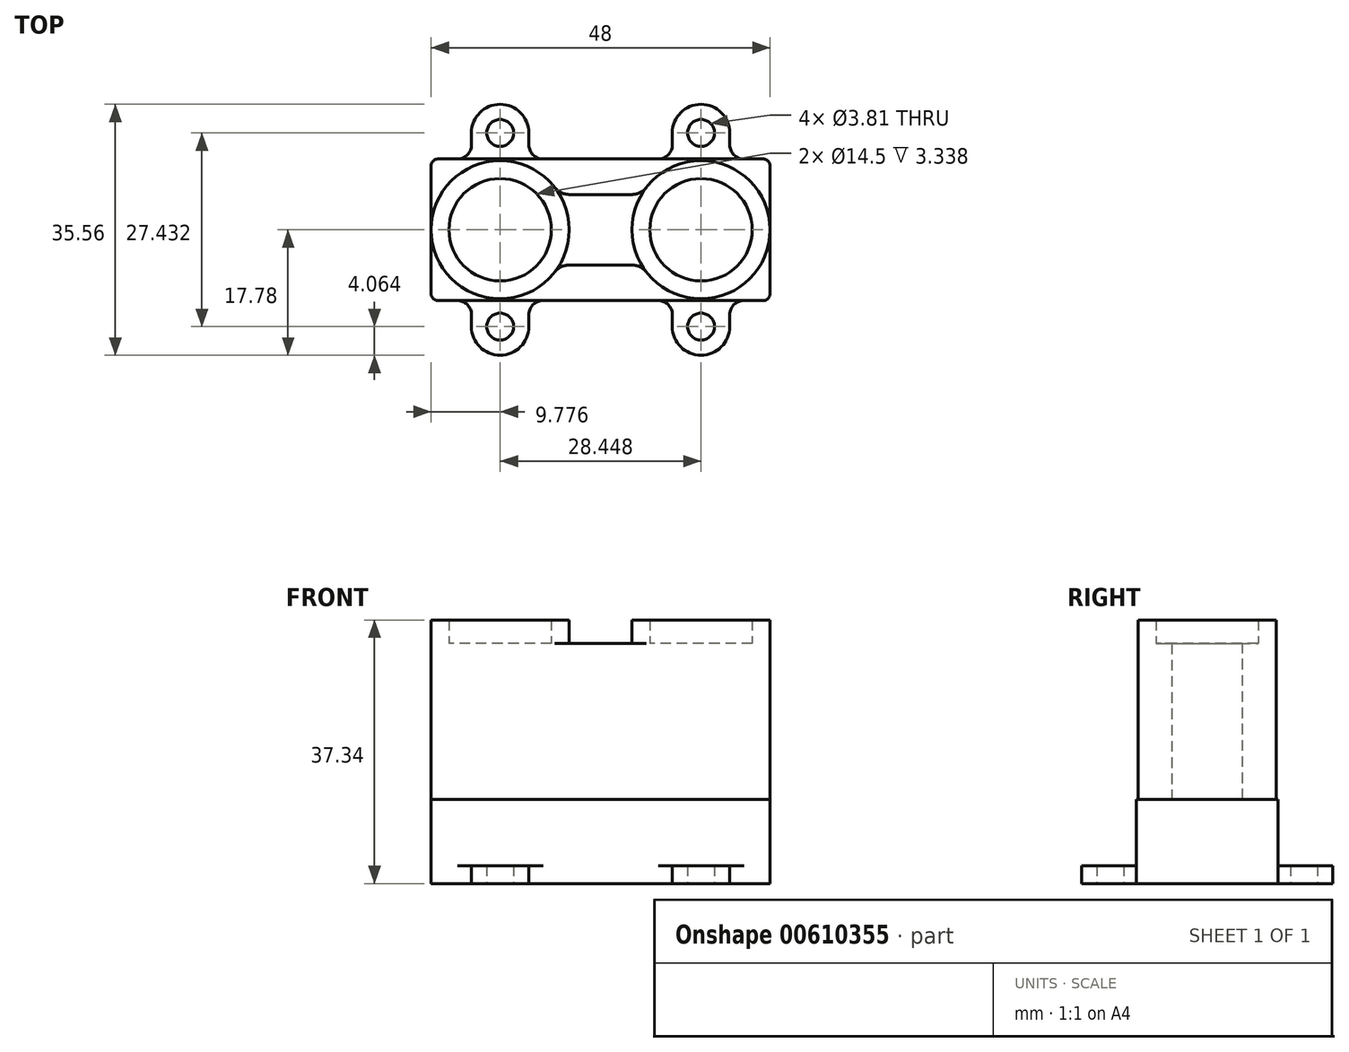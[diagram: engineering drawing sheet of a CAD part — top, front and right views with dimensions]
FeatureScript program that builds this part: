
annotation { "Feature Type Name" : "Feature", "Feature Type Description" : "" }
export const myFeature = defineFeature(function(context is Context, id is Id, definition is map)
    precondition{}
    {
        {
            var Q0;
            Q0=qCreatedBy(makeId("Top.planeOp"),FACE);
            var sketch = newSketch(context, id + "F0", { "sketchPlane" : qUnion([Q0])});
            skLineSegment(sketch, "E0.bottom", {"start": v(24, -10.03) * mm, "end": v(-24, -10.03) * mm});
            skLineSegment(sketch, "E0.top", {"start": v(24, 10.03) * mm, "end": v(-24, 10.03) * mm});
            skLineSegment(sketch, "E0.left", {"start": v(24, -10.03) * mm, "end": v(24, 10.03) * mm});
            skLineSegment(sketch, "E0.right", {"start": v(-24, -10.03) * mm, "end": v(-24, 10.03) * mm});
            skPoint(sketch, "E0.middle", {"position": v(0, 0) * mm});
            skLineSegment(sketch, "E1.bottom", {"start": v(24, -17.78) * mm, "end": v(-24, -17.78) * mm});
            skLineSegment(sketch, "E1.top", {"start": v(24, 17.78) * mm, "end": v(-24, 17.78) * mm});
            skLineSegment(sketch, "E1.left", {"start": v(24, -17.78) * mm, "end": v(24, 17.78) * mm});
            skLineSegment(sketch, "E1.right", {"start": v(-24, -17.78) * mm, "end": v(-24, 17.78) * mm});
            skLineSegment(sketch, "E2.bottom", {"start": v(14.22, -13.72) * mm, "end": v(-14.22, -13.72) * mm, "construction": true});
            skLineSegment(sketch, "E2.top", {"start": v(14.22, 13.72) * mm, "end": v(-14.22, 13.72) * mm, "construction": true});
            skLineSegment(sketch, "E2.left", {"start": v(14.22, -13.72) * mm, "end": v(14.22, 13.72) * mm, "construction": true});
            skLineSegment(sketch, "E2.right", {"start": v(-14.22, -13.72) * mm, "end": v(-14.22, 13.72) * mm, "construction": true});
            skCircle(sketch, "E3", {"center": v(-14.22, 13.72) * mm, "radius": 1.9 * mm});
            skCircle(sketch, "E4", {"center": v(14.22, 13.72) * mm, "radius": 1.9 * mm});
            skCircle(sketch, "E5", {"center": v(14.22, -13.72) * mm, "radius": 1.9 * mm});
            skCircle(sketch, "E6", {"center": v(-14.22, -13.72) * mm, "radius": 1.9 * mm});
            skCircle(sketch, "E7", {"center": v(-14.22, 13.72) * mm, "radius": 4.06 * mm});
            skCircle(sketch, "E8", {"center": v(14.22, 13.72) * mm, "radius": 4.06 * mm});
            skCircle(sketch, "E9", {"center": v(14.22, -13.72) * mm, "radius": 4.06 * mm});
            skCircle(sketch, "E10", {"center": v(-14.22, -13.72) * mm, "radius": 4.06 * mm});
            skLineSegment(sketch, "E11.bottom", {"start": v(-10.16, 13.72) * mm, "end": v(-18.29, 13.72) * mm});
            skLineSegment(sketch, "E11.top", {"start": v(-10.16, 6.35) * mm, "end": v(-18.29, 6.35) * mm});
            skLineSegment(sketch, "E11.left", {"start": v(-10.16, 13.72) * mm, "end": v(-10.16, 6.35) * mm});
            skLineSegment(sketch, "E11.right", {"start": v(-18.29, 13.72) * mm, "end": v(-18.29, 6.35) * mm});
            skPoint(sketch, "E11.middle", {"position": v(-14.22, 10.03) * mm});
            skLineSegment(sketch, "E12.bottom", {"start": v(18.29, 13.72) * mm, "end": v(10.16, 13.72) * mm});
            skLineSegment(sketch, "E12.top", {"start": v(18.29, 6.35) * mm, "end": v(10.16, 6.35) * mm});
            skLineSegment(sketch, "E12.left", {"start": v(18.29, 13.72) * mm, "end": v(18.29, 6.35) * mm});
            skLineSegment(sketch, "E12.right", {"start": v(10.16, 13.72) * mm, "end": v(10.16, 6.35) * mm});
            skPoint(sketch, "E12.middle", {"position": v(14.22, 10.03) * mm});
            skLineSegment(sketch, "E13.bottom", {"start": v(10.16, -13.72) * mm, "end": v(18.29, -13.72) * mm});
            skLineSegment(sketch, "E13.top", {"start": v(10.16, -6.35) * mm, "end": v(18.29, -6.35) * mm});
            skLineSegment(sketch, "E13.left", {"start": v(10.16, -13.72) * mm, "end": v(10.16, -6.35) * mm});
            skLineSegment(sketch, "E13.right", {"start": v(18.29, -13.72) * mm, "end": v(18.29, -6.35) * mm});
            skPoint(sketch, "E13.middle", {"position": v(14.22, -10.03) * mm});
            skLineSegment(sketch, "E14.bottom", {"start": v(-10.16, -13.72) * mm, "end": v(-18.29, -13.72) * mm});
            skLineSegment(sketch, "E14.top", {"start": v(-10.16, -6.35) * mm, "end": v(-18.29, -6.35) * mm});
            skLineSegment(sketch, "E14.left", {"start": v(-10.16, -13.72) * mm, "end": v(-10.16, -6.35) * mm});
            skLineSegment(sketch, "E14.right", {"start": v(-18.29, -13.72) * mm, "end": v(-18.29, -6.35) * mm});
            skPoint(sketch, "E14.middle", {"position": v(-14.22, -10.03) * mm});
            skCircle(sketch, "E15", {"center": v(14.22, 0) * mm, "radius": 9.78 * mm});
            skCircle(sketch, "E16", {"center": v(-14.22, 0) * mm, "radius": 9.78 * mm});
            skLineSegment(sketch, "E17.bottom", {"start": v(9.52, -5) * mm, "end": v(-9.52, -5) * mm});
            skLineSegment(sketch, "E17.top", {"start": v(9.52, 5) * mm, "end": v(-9.52, 5) * mm});
            skLineSegment(sketch, "E17.left", {"start": v(9.52, -5) * mm, "end": v(9.52, 5) * mm});
            skLineSegment(sketch, "E17.right", {"start": v(-9.52, -5) * mm, "end": v(-9.52, 5) * mm});
            skCircle(sketch, "E18", {"center": v(-14.22, 0) * mm, "radius": 7.25 * mm});
            skCircle(sketch, "E19", {"center": v(14.22, 0) * mm, "radius": 7.25 * mm});
            skLineSegment(sketch, "E20", {"start": v(24, -10.03) * mm, "end": v(-3.5, -10.03) * mm, "construction": true});
            skLineSegment(sketch, "E21.bottom", {"start": v(-3.5, -10.03) * mm, "end": v(7.5, -10.03) * mm, "construction": true});
            skLineSegment(sketch, "E21.top", {"start": v(-3.5, -13.03) * mm, "end": v(7.5, -13.03) * mm, "construction": true});
            skLineSegment(sketch, "E21.left", {"start": v(-3.5, -10.03) * mm, "end": v(-3.5, -13.03) * mm, "construction": true});
            skLineSegment(sketch, "E21.right", {"start": v(7.5, -10.03) * mm, "end": v(7.5, -13.03) * mm, "construction": true});
            skSolve(sketch);
        }
        {
            var Q0;
            {var subQ0=sQuery(id+"F0.wireOp",EDGE,"E12.bottom");var subQ3=sQuery(id+"F0.wireOp",EDGE,"E4");var subQ4=makeQuery(id+"F0.imprint","INTERSECT",VERTEX,{"disambiguationData":[OD(0.0)],"derivedFrom":[subQ3,subQ0]});Q0=makeQuery(id+"F0.imprint","IMPRINT",FACE,{"disambiguationData":[TD([[makeQuery(id+"F0.imprint","IMPRINT",EDGE,{"disambiguationData":[TD([[subQ4,-1.0]])],"derivedFrom":subQ3}),-1.0]])]});}
            var Q1;
            {var subQ0=sQuery(id+"F0.wireOp",EDGE,"E11.bottom");var subQ5=sQuery(id+"F0.wireOp",EDGE,"E3");var subQ6=makeQuery(id+"F0.imprint","INTERSECT",VERTEX,{"disambiguationData":[OD(0.0)],"derivedFrom":[subQ5,subQ0]});Q1=makeQuery(id+"F0.imprint","IMPRINT",FACE,{"disambiguationData":[TD([[makeQuery(id+"F0.imprint","IMPRINT",EDGE,{"disambiguationData":[TD([[subQ6,-1.0]])],"derivedFrom":subQ5}),-1.0]])]});}
            var Q2;
            {var subQ0=sQuery(id+"F0.wireOp",EDGE,"E14.bottom");var subQ5=sQuery(id+"F0.wireOp",EDGE,"E6");var subQ6=makeQuery(id+"F0.imprint","INTERSECT",VERTEX,{"disambiguationData":[OD(0.0)],"derivedFrom":[subQ5,subQ0]});Q2=makeQuery(id+"F0.imprint","IMPRINT",FACE,{"disambiguationData":[TD([[makeQuery(id+"F0.imprint","IMPRINT",EDGE,{"disambiguationData":[TD([[subQ6,1.0]])],"derivedFrom":subQ5}),-1.0]])]});}
            var Q3;
            {var subQ0=sQuery(id+"F0.wireOp",EDGE,"E13.bottom");var subQ3=sQuery(id+"F0.wireOp",EDGE,"E5");var subQ4=makeQuery(id+"F0.imprint","INTERSECT",VERTEX,{"disambiguationData":[OD(0.0)],"derivedFrom":[subQ3,subQ0]});Q3=makeQuery(id+"F0.imprint","IMPRINT",FACE,{"disambiguationData":[TD([[makeQuery(id+"F0.imprint","IMPRINT",EDGE,{"disambiguationData":[TD([[subQ4,-1.0]])],"derivedFrom":subQ3}),-1.0]])]});}
            var Q4;
            {var subQ1=sQuery(id+"F0.wireOp",EDGE,"E9");var subQ3=sQuery(id+"F0.wireOp",EDGE,"E0.bottom");var subQ6=makeQuery(id+"F0.imprint","INTERSECT",VERTEX,{"disambiguationData":[OD(0.0)],"derivedFrom":[subQ3,subQ1]});Q4=makeQuery(id+"F0.imprint","IMPRINT",FACE,{"disambiguationData":[TD([[makeQuery(id+"F0.imprint","IMPRINT",EDGE,{"disambiguationData":[TD([[subQ6,-1.0]])],"derivedFrom":subQ3}),1.0]])]});}
            var Q5;
            {var subQ0=sQuery(id+"F0.wireOp",EDGE,"E13.right");var subQ1=sQuery(id+"F0.wireOp",EDGE,"E0.bottom");var subQ2=makeQuery(id+"F0.imprint","INTERSECT",VERTEX,{"derivedFrom":[subQ1,subQ0]});Q5=makeQuery(id+"F0.imprint","IMPRINT",FACE,{"disambiguationData":[TD([[makeQuery(id+"F0.imprint","IMPRINT",EDGE,{"disambiguationData":[TD([[subQ2,-1.0]])],"derivedFrom":subQ1}),1.0]])]});}
            var Q6;
            {var subQ0=sQuery(id+"F0.wireOp",EDGE,"E9");var subQ1=sQuery(id+"F0.wireOp",EDGE,"E0.bottom");var subQ2=makeQuery(id+"F0.imprint","INTERSECT",VERTEX,{"disambiguationData":[OD(1.0)],"derivedFrom":[subQ1,subQ0]});Q6=makeQuery(id+"F0.imprint","IMPRINT",FACE,{"disambiguationData":[TD([[makeQuery(id+"F0.imprint","IMPRINT",EDGE,{"disambiguationData":[TD([[subQ2,-1.0]])],"derivedFrom":subQ1}),1.0]])]});}
            var Q7;
            {var subQ1=sQuery(id+"F0.wireOp",EDGE,"E10");var subQ3=sQuery(id+"F0.wireOp",EDGE,"E0.bottom");var subQ6=makeQuery(id+"F0.imprint","INTERSECT",VERTEX,{"disambiguationData":[OD(0.0)],"derivedFrom":[subQ3,subQ1]});Q7=makeQuery(id+"F0.imprint","IMPRINT",FACE,{"disambiguationData":[TD([[makeQuery(id+"F0.imprint","IMPRINT",EDGE,{"disambiguationData":[TD([[subQ6,-1.0]])],"derivedFrom":subQ3}),1.0]])]});}
            var Q8;
            {var subQ0=sQuery(id+"F0.wireOp",EDGE,"E10");var subQ1=sQuery(id+"F0.wireOp",EDGE,"E0.bottom");var subQ2=makeQuery(id+"F0.imprint","INTERSECT",VERTEX,{"disambiguationData":[OD(1.0)],"derivedFrom":[subQ1,subQ0]});Q8=makeQuery(id+"F0.imprint","IMPRINT",FACE,{"disambiguationData":[TD([[makeQuery(id+"F0.imprint","IMPRINT",EDGE,{"disambiguationData":[TD([[subQ2,-1.0]])],"derivedFrom":subQ1}),1.0]])]});}
            var Q9;
            {var subQ0=sQuery(id+"F0.wireOp",EDGE,"E14.left");var subQ1=sQuery(id+"F0.wireOp",EDGE,"E0.bottom");var subQ2=makeQuery(id+"F0.imprint","INTERSECT",VERTEX,{"derivedFrom":[subQ1,subQ0]});Q9=makeQuery(id+"F0.imprint","IMPRINT",FACE,{"disambiguationData":[TD([[makeQuery(id+"F0.imprint","IMPRINT",EDGE,{"disambiguationData":[TD([[subQ2,-1.0]])],"derivedFrom":subQ1}),1.0]])]});}
            var Q10;
            {var subQ1=sQuery(id+"F0.wireOp",EDGE,"E8");var subQ3=sQuery(id+"F0.wireOp",EDGE,"E0.top");var subQ4=makeQuery(id+"F0.imprint","INTERSECT",VERTEX,{"disambiguationData":[OD(0.0)],"derivedFrom":[subQ3,subQ1]});Q10=makeQuery(id+"F0.imprint","IMPRINT",FACE,{"disambiguationData":[TD([[makeQuery(id+"F0.imprint","IMPRINT",EDGE,{"disambiguationData":[TD([[subQ4,-1.0]])],"derivedFrom":subQ3}),-1.0]])]});}
            var Q11;
            {var subQ1=sQuery(id+"F0.wireOp",EDGE,"E7");var subQ3=sQuery(id+"F0.wireOp",EDGE,"E0.top");var subQ4=makeQuery(id+"F0.imprint","INTERSECT",VERTEX,{"disambiguationData":[OD(0.0)],"derivedFrom":[subQ3,subQ1]});Q11=makeQuery(id+"F0.imprint","IMPRINT",FACE,{"disambiguationData":[TD([[makeQuery(id+"F0.imprint","IMPRINT",EDGE,{"disambiguationData":[TD([[subQ4,-1.0]])],"derivedFrom":subQ3}),-1.0]])]});}
            var Q12;
            {var subQ8=sQuery(id+"F0.wireOp",EDGE,"E11.top");Q12=makeQuery(id+"F0.imprint","IMPRINT",FACE,{"disambiguationData":[TD([[makeQuery(id+"F0.imprint","IMPRINT",EDGE,{"derivedFrom":subQ8}),1.0]])]});}
            var Q13;
            {var subQ0=sQuery(id+"F0.wireOp",EDGE,"E11.top");Q13=makeQuery(id+"F0.imprint","IMPRINT",FACE,{"disambiguationData":[TD([[makeQuery(id+"F0.imprint","IMPRINT",EDGE,{"derivedFrom":subQ0}),-1.0]])]});}
            var Q14;
            {var subQ5=sQuery(id+"F0.wireOp",EDGE,"E14.top");Q14=makeQuery(id+"F0.imprint","IMPRINT",FACE,{"disambiguationData":[TD([[makeQuery(id+"F0.imprint","IMPRINT",EDGE,{"derivedFrom":subQ5}),1.0]])]});}
            var Q15;
            {var subQ0=sQuery(id+"F0.wireOp",EDGE,"E13.top");Q15=makeQuery(id+"F0.imprint","IMPRINT",FACE,{"disambiguationData":[TD([[makeQuery(id+"F0.imprint","IMPRINT",EDGE,{"derivedFrom":subQ0}),-1.0]])]});}
            var Q16;
            {var subQ0=sQuery(id+"F0.wireOp",EDGE,"E12.top");Q16=makeQuery(id+"F0.imprint","IMPRINT",FACE,{"disambiguationData":[TD([[makeQuery(id+"F0.imprint","IMPRINT",EDGE,{"derivedFrom":subQ0}),-1.0]])]});}
            var Q17;
            {var subQ0=sQuery(id+"F0.wireOp",EDGE,"E8");var subQ1=sQuery(id+"F0.wireOp",EDGE,"E0.top");var subQ2=makeQuery(id+"F0.imprint","INTERSECT",VERTEX,{"disambiguationData":[OD(1.0)],"derivedFrom":[subQ1,subQ0]});Q17=makeQuery(id+"F0.imprint","IMPRINT",FACE,{"disambiguationData":[TD([[makeQuery(id+"F0.imprint","IMPRINT",EDGE,{"disambiguationData":[TD([[subQ2,-1.0]])],"derivedFrom":subQ1}),-1.0]])]});}
            var Q18;
            {var subQ0=sQuery(id+"F0.wireOp",EDGE,"E12.left");var subQ1=sQuery(id+"F0.wireOp",EDGE,"E0.top");var subQ2=makeQuery(id+"F0.imprint","INTERSECT",VERTEX,{"derivedFrom":[subQ1,subQ0]});Q18=makeQuery(id+"F0.imprint","IMPRINT",FACE,{"disambiguationData":[TD([[makeQuery(id+"F0.imprint","IMPRINT",EDGE,{"disambiguationData":[TD([[subQ2,-1.0]])],"derivedFrom":subQ1}),-1.0]])]});}
            var Q19;
            {var subQ0=sQuery(id+"F0.wireOp",EDGE,"E8");var subQ1=sQuery(id+"F0.wireOp",EDGE,"E0.top");var subQ2=makeQuery(id+"F0.imprint","INTERSECT",VERTEX,{"disambiguationData":[OD(0.0)],"derivedFrom":[subQ1,subQ0]});Q19=makeQuery(id+"F0.imprint","IMPRINT",FACE,{"disambiguationData":[TD([[makeQuery(id+"F0.imprint","IMPRINT",EDGE,{"disambiguationData":[TD([[subQ2,-1.0]])],"derivedFrom":subQ1}),1.0]])]});}
            var Q20;
            {var subQ0=sQuery(id+"F0.wireOp",EDGE,"E9");var subQ1=sQuery(id+"F0.wireOp",EDGE,"E0.bottom");var subQ2=makeQuery(id+"F0.imprint","INTERSECT",VERTEX,{"disambiguationData":[OD(0.0)],"derivedFrom":[subQ1,subQ0]});Q20=makeQuery(id+"F0.imprint","IMPRINT",FACE,{"disambiguationData":[TD([[makeQuery(id+"F0.imprint","IMPRINT",EDGE,{"disambiguationData":[TD([[subQ2,-1.0]])],"derivedFrom":subQ1}),-1.0]])]});}
            var Q21;
            {var subQ0=sQuery(id+"F0.wireOp",EDGE,"E10");var subQ1=sQuery(id+"F0.wireOp",EDGE,"E0.bottom");var subQ2=makeQuery(id+"F0.imprint","INTERSECT",VERTEX,{"disambiguationData":[OD(0.0)],"derivedFrom":[subQ1,subQ0]});Q21=makeQuery(id+"F0.imprint","IMPRINT",FACE,{"disambiguationData":[TD([[makeQuery(id+"F0.imprint","IMPRINT",EDGE,{"disambiguationData":[TD([[subQ2,-1.0]])],"derivedFrom":subQ1}),-1.0]])]});}
            var Q22;
            {var subQ0=sQuery(id+"F0.wireOp",EDGE,"E7");var subQ1=sQuery(id+"F0.wireOp",EDGE,"E0.top");var subQ2=makeQuery(id+"F0.imprint","INTERSECT",VERTEX,{"disambiguationData":[OD(0.0)],"derivedFrom":[subQ1,subQ0]});Q22=makeQuery(id+"F0.imprint","IMPRINT",FACE,{"disambiguationData":[TD([[makeQuery(id+"F0.imprint","IMPRINT",EDGE,{"disambiguationData":[TD([[subQ2,-1.0]])],"derivedFrom":subQ1}),1.0]])]});}
            var Q23;
            {var subQ0=sQuery(id+"F0.wireOp",EDGE,"E7");var subQ1=sQuery(id+"F0.wireOp",EDGE,"E0.top");var subQ2=makeQuery(id+"F0.imprint","INTERSECT",VERTEX,{"disambiguationData":[OD(1.0)],"derivedFrom":[subQ1,subQ0]});Q23=makeQuery(id+"F0.imprint","IMPRINT",FACE,{"disambiguationData":[TD([[makeQuery(id+"F0.imprint","IMPRINT",EDGE,{"disambiguationData":[TD([[subQ2,-1.0]])],"derivedFrom":subQ1}),-1.0]])]});}
            var Q24;
            {var subQ0=sQuery(id+"F0.wireOp",EDGE,"E11.left");var subQ1=sQuery(id+"F0.wireOp",EDGE,"E0.top");var subQ2=makeQuery(id+"F0.imprint","INTERSECT",VERTEX,{"derivedFrom":[subQ1,subQ0]});Q24=makeQuery(id+"F0.imprint","IMPRINT",FACE,{"disambiguationData":[TD([[makeQuery(id+"F0.imprint","IMPRINT",EDGE,{"disambiguationData":[TD([[subQ2,-1.0]])],"derivedFrom":subQ1}),-1.0]])]});}
            var Q25;
            {var subQ5=sQuery(id+"F0.wireOp",EDGE,"E17.right");Q25=makeQuery(id+"F0.imprint","IMPRINT",FACE,{"disambiguationData":[TD([[makeQuery(id+"F0.imprint","IMPRINT",EDGE,{"derivedFrom":subQ5}),-1.0]])]});}
            var Q26;
            {var subQ1=sQuery(id+"F0.wireOp",EDGE,"E12.right");var subQ5=sQuery(id+"F0.wireOp",EDGE,"E0.top");var subQ6=makeQuery(id+"F0.imprint","INTERSECT",VERTEX,{"derivedFrom":[subQ5,subQ1]});Q26=makeQuery(id+"F0.imprint","IMPRINT",FACE,{"disambiguationData":[TD([[makeQuery(id+"F0.imprint","IMPRINT",EDGE,{"disambiguationData":[TD([[subQ6,-1.0]])],"derivedFrom":subQ5}),1.0]])]});}
            var Q27;
            {var subQ5=sQuery(id+"F0.wireOp",EDGE,"E17.left");Q27=makeQuery(id+"F0.imprint","IMPRINT",FACE,{"disambiguationData":[TD([[makeQuery(id+"F0.imprint","IMPRINT",EDGE,{"derivedFrom":subQ5}),1.0]])]});}
            var Q28;
            {var subQ0=sQuery(id+"F0.wireOp",EDGE,"E17.top");var subQ1=sQuery(id+"F0.wireOp",EDGE,"E15");var subQ2=makeQuery(id+"F0.imprint","INTERSECT",VERTEX,{"derivedFrom":[subQ1,subQ0]});Q28=makeQuery(id+"F0.imprint","IMPRINT",FACE,{"disambiguationData":[TD([[makeQuery(id+"F0.imprint","IMPRINT",EDGE,{"disambiguationData":[TD([[subQ2,-1.0]])],"derivedFrom":subQ1}),-1.0]])]});}
            var Q29;
            {var subQ1=sQuery(id+"F0.wireOp",EDGE,"E0.bottom");var subQ6=sQuery(id+"F0.wireOp",EDGE,"E13.left");var subQ10=makeQuery(id+"F0.imprint","INTERSECT",VERTEX,{"derivedFrom":[subQ1,subQ6]});Q29=makeQuery(id+"F0.imprint","IMPRINT",FACE,{"disambiguationData":[TD([[makeQuery(id+"F0.imprint","IMPRINT",EDGE,{"disambiguationData":[TD([[subQ10,-1.0]])],"derivedFrom":subQ1}),-1.0]])]});}
            var Q30;
            {var subQ15=sQuery(id+"F0.wireOp",EDGE,"E12.top");Q30=makeQuery(id+"F0.imprint","IMPRINT",FACE,{"disambiguationData":[TD([[makeQuery(id+"F0.imprint","IMPRINT",EDGE,{"derivedFrom":subQ15}),1.0]])]});}
            var Q31;
            {var subQ0=sQuery(id+"F0.wireOp",EDGE,"E7");var subQ1=sQuery(id+"F0.wireOp",EDGE,"E0.top");var subQ2=makeQuery(id+"F0.imprint","INTERSECT",VERTEX,{"disambiguationData":[OD(1.0)],"derivedFrom":[subQ1,subQ0]});Q31=makeQuery(id+"F0.imprint","IMPRINT",FACE,{"disambiguationData":[TD([[makeQuery(id+"F0.imprint","IMPRINT",EDGE,{"disambiguationData":[TD([[subQ2,-1.0]])],"derivedFrom":subQ1}),1.0]])]});}
            var Q32;
            {var subQ0=sQuery(id+"F0.wireOp",EDGE,"E16");var subQ1=sQuery(id+"F0.wireOp",EDGE,"E7");var subQ2=makeQuery(id+"F0.imprint","INTERSECT",VERTEX,{"disambiguationData":[OD(0.0)],"derivedFrom":[subQ1,subQ0]});Q32=makeQuery(id+"F0.imprint","IMPRINT",FACE,{"disambiguationData":[TD([[makeQuery(id+"F0.imprint","IMPRINT",EDGE,{"disambiguationData":[TD([[subQ2,-1.0]])],"derivedFrom":subQ1}),1.0]])]});}
            var Q33;
            {var subQ0=sQuery(id+"F0.wireOp",EDGE,"E11.left");var subQ1=sQuery(id+"F0.wireOp",EDGE,"E0.top");var subQ2=makeQuery(id+"F0.imprint","INTERSECT",VERTEX,{"derivedFrom":[subQ1,subQ0]});Q33=makeQuery(id+"F0.imprint","IMPRINT",FACE,{"disambiguationData":[TD([[makeQuery(id+"F0.imprint","IMPRINT",EDGE,{"disambiguationData":[TD([[subQ2,-1.0]])],"derivedFrom":subQ1}),1.0]])]});}
            var Q34;
            {var subQ0=sQuery(id+"F0.wireOp",EDGE,"E10");var subQ1=sQuery(id+"F0.wireOp",EDGE,"E0.bottom");var subQ2=makeQuery(id+"F0.imprint","INTERSECT",VERTEX,{"disambiguationData":[OD(1.0)],"derivedFrom":[subQ1,subQ0]});Q34=makeQuery(id+"F0.imprint","IMPRINT",FACE,{"disambiguationData":[TD([[makeQuery(id+"F0.imprint","IMPRINT",EDGE,{"disambiguationData":[TD([[subQ2,-1.0]])],"derivedFrom":subQ1}),-1.0]])]});}
            var Q35;
            {var subQ0=sQuery(id+"F0.wireOp",EDGE,"E16");var subQ1=sQuery(id+"F0.wireOp",EDGE,"E10");var subQ2=makeQuery(id+"F0.imprint","INTERSECT",VERTEX,{"disambiguationData":[OD(0.0)],"derivedFrom":[subQ1,subQ0]});Q35=makeQuery(id+"F0.imprint","IMPRINT",FACE,{"disambiguationData":[TD([[makeQuery(id+"F0.imprint","IMPRINT",EDGE,{"disambiguationData":[TD([[subQ2,-1.0]])],"derivedFrom":subQ1}),1.0]])]});}
            var Q36;
            {var subQ0=sQuery(id+"F0.wireOp",EDGE,"E14.left");var subQ1=sQuery(id+"F0.wireOp",EDGE,"E0.bottom");var subQ2=makeQuery(id+"F0.imprint","INTERSECT",VERTEX,{"derivedFrom":[subQ1,subQ0]});Q36=makeQuery(id+"F0.imprint","IMPRINT",FACE,{"disambiguationData":[TD([[makeQuery(id+"F0.imprint","IMPRINT",EDGE,{"disambiguationData":[TD([[subQ2,-1.0]])],"derivedFrom":subQ1}),-1.0]])]});}
            var Q37;
            {var subQ0=sQuery(id+"F0.wireOp",EDGE,"E13.right");var subQ1=sQuery(id+"F0.wireOp",EDGE,"E0.bottom");var subQ2=makeQuery(id+"F0.imprint","INTERSECT",VERTEX,{"derivedFrom":[subQ1,subQ0]});Q37=makeQuery(id+"F0.imprint","IMPRINT",FACE,{"disambiguationData":[TD([[makeQuery(id+"F0.imprint","IMPRINT",EDGE,{"disambiguationData":[TD([[subQ2,-1.0]])],"derivedFrom":subQ1}),-1.0]])]});}
            var Q38;
            {var subQ0=sQuery(id+"F0.wireOp",EDGE,"E9");var subQ1=sQuery(id+"F0.wireOp",EDGE,"E0.bottom");var subQ2=makeQuery(id+"F0.imprint","INTERSECT",VERTEX,{"disambiguationData":[OD(1.0)],"derivedFrom":[subQ1,subQ0]});Q38=makeQuery(id+"F0.imprint","IMPRINT",FACE,{"disambiguationData":[TD([[makeQuery(id+"F0.imprint","IMPRINT",EDGE,{"disambiguationData":[TD([[subQ2,-1.0]])],"derivedFrom":subQ1}),-1.0]])]});}
            var Q39;
            {var subQ0=sQuery(id+"F0.wireOp",EDGE,"E15");var subQ1=sQuery(id+"F0.wireOp",EDGE,"E9");var subQ2=makeQuery(id+"F0.imprint","INTERSECT",VERTEX,{"disambiguationData":[OD(0.0)],"derivedFrom":[subQ1,subQ0]});Q39=makeQuery(id+"F0.imprint","IMPRINT",FACE,{"disambiguationData":[TD([[makeQuery(id+"F0.imprint","IMPRINT",EDGE,{"disambiguationData":[TD([[subQ2,-1.0]])],"derivedFrom":subQ1}),1.0]])]});}
            var Q40;
            {var subQ0=sQuery(id+"F0.wireOp",EDGE,"E15");var subQ1=sQuery(id+"F0.wireOp",EDGE,"E8");var subQ2=makeQuery(id+"F0.imprint","INTERSECT",VERTEX,{"disambiguationData":[OD(0.0)],"derivedFrom":[subQ1,subQ0]});Q40=makeQuery(id+"F0.imprint","IMPRINT",FACE,{"disambiguationData":[TD([[makeQuery(id+"F0.imprint","IMPRINT",EDGE,{"disambiguationData":[TD([[subQ2,-1.0]])],"derivedFrom":subQ1}),1.0]])]});}
            var Q41;
            {var subQ0=sQuery(id+"F0.wireOp",EDGE,"E8");var subQ1=sQuery(id+"F0.wireOp",EDGE,"E0.top");var subQ2=makeQuery(id+"F0.imprint","INTERSECT",VERTEX,{"disambiguationData":[OD(1.0)],"derivedFrom":[subQ1,subQ0]});Q41=makeQuery(id+"F0.imprint","IMPRINT",FACE,{"disambiguationData":[TD([[makeQuery(id+"F0.imprint","IMPRINT",EDGE,{"disambiguationData":[TD([[subQ2,-1.0]])],"derivedFrom":subQ1}),1.0]])]});}
            var Q42;
            {var subQ0=sQuery(id+"F0.wireOp",EDGE,"E12.left");var subQ1=sQuery(id+"F0.wireOp",EDGE,"E0.top");var subQ2=makeQuery(id+"F0.imprint","INTERSECT",VERTEX,{"derivedFrom":[subQ1,subQ0]});Q42=makeQuery(id+"F0.imprint","IMPRINT",FACE,{"disambiguationData":[TD([[makeQuery(id+"F0.imprint","IMPRINT",EDGE,{"disambiguationData":[TD([[subQ2,-1.0]])],"derivedFrom":subQ1}),1.0]])]});}
            var Q43;
            {var subQ0=sQuery(id+"F0.wireOp",EDGE,"E1.left");var subQ1=sQuery(id+"F0.wireOp",EDGE,"E0.bottom");var subQ2=makeQuery(id+"F0.imprint","INTERSECT",VERTEX,{"derivedFrom":[subQ1,subQ0]});Q43=makeQuery(id+"F0.imprint","IMPRINT",FACE,{"disambiguationData":[TD([[makeQuery(id+"F0.imprint","IMPRINT",EDGE,{"disambiguationData":[TD([[subQ2,-1.0]])],"derivedFrom":subQ1}),-1.0]])]});}
            var Q44;
            {var subQ0=sQuery(id+"F0.wireOp",EDGE,"E1.left");var subQ1=sQuery(id+"F0.wireOp",EDGE,"E0.top");var subQ2=makeQuery(id+"F0.imprint","INTERSECT",VERTEX,{"derivedFrom":[subQ1,subQ0]});Q44=makeQuery(id+"F0.imprint","IMPRINT",FACE,{"disambiguationData":[TD([[makeQuery(id+"F0.imprint","IMPRINT",EDGE,{"disambiguationData":[TD([[subQ2,-1.0]])],"derivedFrom":subQ1}),1.0]])]});}
            var Q45;
            {var subQ0=sQuery(id+"F0.wireOp",EDGE,"E1.right");var subQ1=sQuery(id+"F0.wireOp",EDGE,"E0.bottom");var subQ2=makeQuery(id+"F0.imprint","INTERSECT",VERTEX,{"derivedFrom":[subQ1,subQ0]});Q45=makeQuery(id+"F0.imprint","IMPRINT",FACE,{"disambiguationData":[TD([[makeQuery(id+"F0.imprint","IMPRINT",EDGE,{"disambiguationData":[TD([[subQ2,1.0]])],"derivedFrom":subQ1}),-1.0]])]});}
            var Q46;
            {var subQ0=sQuery(id+"F0.wireOp",EDGE,"E1.right");var subQ1=sQuery(id+"F0.wireOp",EDGE,"E0.top");var subQ2=makeQuery(id+"F0.imprint","INTERSECT",VERTEX,{"derivedFrom":[subQ1,subQ0]});Q46=makeQuery(id+"F0.imprint","IMPRINT",FACE,{"disambiguationData":[TD([[makeQuery(id+"F0.imprint","IMPRINT",EDGE,{"disambiguationData":[TD([[subQ2,1.0]])],"derivedFrom":subQ1}),1.0]])]});}
            var Q47;
            {var subQ8=sQuery(id+"F0.wireOp",EDGE,"E11.right");var subQ10=sQuery(id+"F0.wireOp",EDGE,"E11.top");var subQ11=makeQuery(id+"F0.imprint","INTERSECT",VERTEX,{"derivedFrom":[subQ10,subQ8]});Q47=makeQuery(id+"F0.imprint","IMPRINT",FACE,{"disambiguationData":[TD([[makeQuery(id+"F0.imprint","IMPRINT",EDGE,{"disambiguationData":[TD([[subQ11,1.0]])],"derivedFrom":subQ10}),1.0]])]});}
            var Q48;
            {var subQ0=sQuery(id+"F0.wireOp",EDGE,"E17.top");var subQ1=sQuery(id+"F0.wireOp",EDGE,"E16");var subQ2=makeQuery(id+"F0.imprint","INTERSECT",VERTEX,{"derivedFrom":[subQ1,subQ0]});Q48=makeQuery(id+"F0.imprint","IMPRINT",FACE,{"disambiguationData":[TD([[makeQuery(id+"F0.imprint","IMPRINT",EDGE,{"disambiguationData":[TD([[subQ2,1.0]])],"derivedFrom":subQ1}),1.0]])]});}
            var Q49;
            {var subQ6=sQuery(id+"F0.wireOp",EDGE,"E17.right");Q49=makeQuery(id+"F0.imprint","IMPRINT",FACE,{"disambiguationData":[TD([[makeQuery(id+"F0.imprint","IMPRINT",EDGE,{"derivedFrom":subQ6}),1.0]])]});}
            var Q50;
            {var subQ0=sQuery(id+"F0.wireOp",EDGE,"E18");var subQ1=sQuery(id+"F0.wireOp",EDGE,"E14.top");var subQ2=makeQuery(id+"F0.imprint","INTERSECT",VERTEX,{"disambiguationData":[OD(0.0)],"derivedFrom":[subQ1,subQ0]});Q50=makeQuery(id+"F0.imprint","IMPRINT",FACE,{"disambiguationData":[TD([[makeQuery(id+"F0.imprint","IMPRINT",EDGE,{"disambiguationData":[TD([[subQ2,-1.0]])],"derivedFrom":subQ1}),1.0]])]});}
            var Q51;
            {var subQ0=sQuery(id+"F0.wireOp",EDGE,"E18");var subQ1=sQuery(id+"F0.wireOp",EDGE,"E11.top");var subQ2=makeQuery(id+"F0.imprint","INTERSECT",VERTEX,{"disambiguationData":[OD(0.0)],"derivedFrom":[subQ1,subQ0]});Q51=makeQuery(id+"F0.imprint","IMPRINT",FACE,{"disambiguationData":[TD([[makeQuery(id+"F0.imprint","IMPRINT",EDGE,{"disambiguationData":[TD([[subQ2,-1.0]])],"derivedFrom":subQ1}),-1.0]])]});}
            var Q52;
            {var subQ5=sQuery(id+"F0.wireOp",EDGE,"E14.left");var subQ7=sQuery(id+"F0.wireOp",EDGE,"E14.top");var subQ8=makeQuery(id+"F0.imprint","INTERSECT",VERTEX,{"derivedFrom":[subQ7,subQ5]});Q52=makeQuery(id+"F0.imprint","IMPRINT",FACE,{"disambiguationData":[TD([[makeQuery(id+"F0.imprint","IMPRINT",EDGE,{"disambiguationData":[TD([[subQ8,-1.0]])],"derivedFrom":subQ7}),-1.0]])]});}
            var Q53;
            {var subQ0=sQuery(id+"F0.wireOp",EDGE,"E17.top");var subQ1=sQuery(id+"F0.wireOp",EDGE,"E15");var subQ2=makeQuery(id+"F0.imprint","INTERSECT",VERTEX,{"derivedFrom":[subQ1,subQ0]});Q53=makeQuery(id+"F0.imprint","IMPRINT",FACE,{"disambiguationData":[TD([[makeQuery(id+"F0.imprint","IMPRINT",EDGE,{"disambiguationData":[TD([[subQ2,-1.0]])],"derivedFrom":subQ1}),1.0]])]});}
            var Q54;
            {var subQ5=sQuery(id+"F0.wireOp",EDGE,"E13.left");var subQ6=sQuery(id+"F0.wireOp",EDGE,"E13.top");var subQ7=makeQuery(id+"F0.imprint","INTERSECT",VERTEX,{"derivedFrom":[subQ6,subQ5]});Q54=makeQuery(id+"F0.imprint","IMPRINT",FACE,{"disambiguationData":[TD([[makeQuery(id+"F0.imprint","IMPRINT",EDGE,{"disambiguationData":[TD([[subQ7,-1.0]])],"derivedFrom":subQ6}),1.0]])]});}
            var Q55;
            {var subQ0=sQuery(id+"F0.wireOp",EDGE,"E19");var subQ1=sQuery(id+"F0.wireOp",EDGE,"E13.top");var subQ2=makeQuery(id+"F0.imprint","INTERSECT",VERTEX,{"disambiguationData":[OD(0.0)],"derivedFrom":[subQ1,subQ0]});Q55=makeQuery(id+"F0.imprint","IMPRINT",FACE,{"disambiguationData":[TD([[makeQuery(id+"F0.imprint","IMPRINT",EDGE,{"disambiguationData":[TD([[subQ2,-1.0]])],"derivedFrom":subQ1}),-1.0]])]});}
            var Q56;
            {var subQ0=sQuery(id+"F0.wireOp",EDGE,"E17.left");Q56=makeQuery(id+"F0.imprint","IMPRINT",FACE,{"disambiguationData":[TD([[makeQuery(id+"F0.imprint","IMPRINT",EDGE,{"derivedFrom":subQ0}),-1.0]])]});}
            var Q57;
            {var subQ0=sQuery(id+"F0.wireOp",EDGE,"E19");var subQ1=sQuery(id+"F0.wireOp",EDGE,"E12.top");var subQ2=makeQuery(id+"F0.imprint","INTERSECT",VERTEX,{"disambiguationData":[OD(0.0)],"derivedFrom":[subQ1,subQ0]});Q57=makeQuery(id+"F0.imprint","IMPRINT",FACE,{"disambiguationData":[TD([[makeQuery(id+"F0.imprint","IMPRINT",EDGE,{"disambiguationData":[TD([[subQ2,-1.0]])],"derivedFrom":subQ1}),-1.0]])]});}
            var Q58;
            {var subQ7=sQuery(id+"F0.wireOp",EDGE,"E12.left");var subQ8=sQuery(id+"F0.wireOp",EDGE,"E12.top");var subQ9=makeQuery(id+"F0.imprint","INTERSECT",VERTEX,{"derivedFrom":[subQ8,subQ7]});Q58=makeQuery(id+"F0.imprint","IMPRINT",FACE,{"disambiguationData":[TD([[makeQuery(id+"F0.imprint","IMPRINT",EDGE,{"disambiguationData":[TD([[subQ9,-1.0]])],"derivedFrom":subQ8}),1.0]])]});}
            extrude(context, id + "F1", {"entities" : qUnion([Q0, Q1, Q2, Q3, Q4, Q5, Q6, Q7, Q8, Q9, Q10, Q11, Q12, Q13, Q14, Q15, Q16, Q17, Q18, Q19, Q20, Q21, Q22, Q23, Q24, Q25, Q26, Q27, Q28, Q29, Q30, Q31, Q32, Q33, Q34, Q35, Q36, Q37, Q38, Q39, Q40, Q41, Q42, Q43, Q44, Q45, Q46, Q47, Q48, Q49, Q50, Q51, Q52, Q53, Q54, Q55, Q56, Q57, Q58]), "depth" : 2.54 * mm, "offsetDistance" : 25.4 * mm});
        }
        {
            var Q0;
            {var subQ8=sQuery(id+"F0.wireOp",EDGE,"E11.top");Q0=makeQuery(id+"F0.imprint","IMPRINT",FACE,{"disambiguationData":[TD([[makeQuery(id+"F0.imprint","IMPRINT",EDGE,{"derivedFrom":subQ8}),1.0]])]});}
            var Q1;
            {var subQ5=sQuery(id+"F0.wireOp",EDGE,"E14.top");Q1=makeQuery(id+"F0.imprint","IMPRINT",FACE,{"disambiguationData":[TD([[makeQuery(id+"F0.imprint","IMPRINT",EDGE,{"derivedFrom":subQ5}),1.0]])]});}
            var Q2;
            {var subQ0=sQuery(id+"F0.wireOp",EDGE,"E13.top");Q2=makeQuery(id+"F0.imprint","IMPRINT",FACE,{"disambiguationData":[TD([[makeQuery(id+"F0.imprint","IMPRINT",EDGE,{"derivedFrom":subQ0}),-1.0]])]});}
            var Q3;
            {var subQ0=sQuery(id+"F0.wireOp",EDGE,"E12.top");Q3=makeQuery(id+"F0.imprint","IMPRINT",FACE,{"disambiguationData":[TD([[makeQuery(id+"F0.imprint","IMPRINT",EDGE,{"derivedFrom":subQ0}),-1.0]])]});}
            var Q4;
            {var subQ0=sQuery(id+"F0.wireOp",EDGE,"E9");var subQ1=sQuery(id+"F0.wireOp",EDGE,"E0.bottom");var subQ2=makeQuery(id+"F0.imprint","INTERSECT",VERTEX,{"disambiguationData":[OD(0.0)],"derivedFrom":[subQ1,subQ0]});Q4=makeQuery(id+"F0.imprint","IMPRINT",FACE,{"disambiguationData":[TD([[makeQuery(id+"F0.imprint","IMPRINT",EDGE,{"disambiguationData":[TD([[subQ2,-1.0]])],"derivedFrom":subQ1}),-1.0]])]});}
            var Q5;
            {var subQ0=sQuery(id+"F0.wireOp",EDGE,"E8");var subQ1=sQuery(id+"F0.wireOp",EDGE,"E0.top");var subQ2=makeQuery(id+"F0.imprint","INTERSECT",VERTEX,{"disambiguationData":[OD(0.0)],"derivedFrom":[subQ1,subQ0]});Q5=makeQuery(id+"F0.imprint","IMPRINT",FACE,{"disambiguationData":[TD([[makeQuery(id+"F0.imprint","IMPRINT",EDGE,{"disambiguationData":[TD([[subQ2,-1.0]])],"derivedFrom":subQ1}),1.0]])]});}
            var Q6;
            {var subQ0=sQuery(id+"F0.wireOp",EDGE,"E10");var subQ1=sQuery(id+"F0.wireOp",EDGE,"E0.bottom");var subQ2=makeQuery(id+"F0.imprint","INTERSECT",VERTEX,{"disambiguationData":[OD(0.0)],"derivedFrom":[subQ1,subQ0]});Q6=makeQuery(id+"F0.imprint","IMPRINT",FACE,{"disambiguationData":[TD([[makeQuery(id+"F0.imprint","IMPRINT",EDGE,{"disambiguationData":[TD([[subQ2,-1.0]])],"derivedFrom":subQ1}),-1.0]])]});}
            var Q7;
            {var subQ0=sQuery(id+"F0.wireOp",EDGE,"E7");var subQ1=sQuery(id+"F0.wireOp",EDGE,"E0.top");var subQ2=makeQuery(id+"F0.imprint","INTERSECT",VERTEX,{"disambiguationData":[OD(0.0)],"derivedFrom":[subQ1,subQ0]});Q7=makeQuery(id+"F0.imprint","IMPRINT",FACE,{"disambiguationData":[TD([[makeQuery(id+"F0.imprint","IMPRINT",EDGE,{"disambiguationData":[TD([[subQ2,-1.0]])],"derivedFrom":subQ1}),1.0]])]});}
            var Q8;
            {var subQ0=sQuery(id+"F0.wireOp",EDGE,"E1.right");var subQ1=sQuery(id+"F0.wireOp",EDGE,"E0.top");var subQ2=makeQuery(id+"F0.imprint","INTERSECT",VERTEX,{"derivedFrom":[subQ1,subQ0]});Q8=makeQuery(id+"F0.imprint","IMPRINT",FACE,{"disambiguationData":[TD([[makeQuery(id+"F0.imprint","IMPRINT",EDGE,{"disambiguationData":[TD([[subQ2,1.0]])],"derivedFrom":subQ1}),1.0]])]});}
            var Q9;
            {var subQ0=sQuery(id+"F0.wireOp",EDGE,"E1.right");var subQ1=sQuery(id+"F0.wireOp",EDGE,"E0.bottom");var subQ2=makeQuery(id+"F0.imprint","INTERSECT",VERTEX,{"derivedFrom":[subQ1,subQ0]});Q9=makeQuery(id+"F0.imprint","IMPRINT",FACE,{"disambiguationData":[TD([[makeQuery(id+"F0.imprint","IMPRINT",EDGE,{"disambiguationData":[TD([[subQ2,1.0]])],"derivedFrom":subQ1}),-1.0]])]});}
            var Q10;
            {var subQ1=sQuery(id+"F0.wireOp",EDGE,"E0.bottom");var subQ6=sQuery(id+"F0.wireOp",EDGE,"E13.left");var subQ10=makeQuery(id+"F0.imprint","INTERSECT",VERTEX,{"derivedFrom":[subQ1,subQ6]});Q10=makeQuery(id+"F0.imprint","IMPRINT",FACE,{"disambiguationData":[TD([[makeQuery(id+"F0.imprint","IMPRINT",EDGE,{"disambiguationData":[TD([[subQ10,-1.0]])],"derivedFrom":subQ1}),-1.0]])]});}
            var Q11;
            {var subQ5=sQuery(id+"F0.wireOp",EDGE,"E17.right");Q11=makeQuery(id+"F0.imprint","IMPRINT",FACE,{"disambiguationData":[TD([[makeQuery(id+"F0.imprint","IMPRINT",EDGE,{"derivedFrom":subQ5}),-1.0]])]});}
            var Q12;
            {var subQ0=sQuery(id+"F0.wireOp",EDGE,"E17.top");var subQ1=sQuery(id+"F0.wireOp",EDGE,"E15");var subQ2=makeQuery(id+"F0.imprint","INTERSECT",VERTEX,{"derivedFrom":[subQ1,subQ0]});Q12=makeQuery(id+"F0.imprint","IMPRINT",FACE,{"disambiguationData":[TD([[makeQuery(id+"F0.imprint","IMPRINT",EDGE,{"disambiguationData":[TD([[subQ2,-1.0]])],"derivedFrom":subQ1}),-1.0]])]});}
            var Q13;
            {var subQ5=sQuery(id+"F0.wireOp",EDGE,"E17.left");Q13=makeQuery(id+"F0.imprint","IMPRINT",FACE,{"disambiguationData":[TD([[makeQuery(id+"F0.imprint","IMPRINT",EDGE,{"derivedFrom":subQ5}),1.0]])]});}
            var Q14;
            {var subQ15=sQuery(id+"F0.wireOp",EDGE,"E12.top");Q14=makeQuery(id+"F0.imprint","IMPRINT",FACE,{"disambiguationData":[TD([[makeQuery(id+"F0.imprint","IMPRINT",EDGE,{"derivedFrom":subQ15}),1.0]])]});}
            var Q15;
            {var subQ0=sQuery(id+"F0.wireOp",EDGE,"E1.left");var subQ1=sQuery(id+"F0.wireOp",EDGE,"E0.top");var subQ2=makeQuery(id+"F0.imprint","INTERSECT",VERTEX,{"derivedFrom":[subQ1,subQ0]});Q15=makeQuery(id+"F0.imprint","IMPRINT",FACE,{"disambiguationData":[TD([[makeQuery(id+"F0.imprint","IMPRINT",EDGE,{"disambiguationData":[TD([[subQ2,-1.0]])],"derivedFrom":subQ1}),1.0]])]});}
            var Q16;
            {var subQ0=sQuery(id+"F0.wireOp",EDGE,"E1.left");var subQ1=sQuery(id+"F0.wireOp",EDGE,"E0.bottom");var subQ2=makeQuery(id+"F0.imprint","INTERSECT",VERTEX,{"derivedFrom":[subQ1,subQ0]});Q16=makeQuery(id+"F0.imprint","IMPRINT",FACE,{"disambiguationData":[TD([[makeQuery(id+"F0.imprint","IMPRINT",EDGE,{"disambiguationData":[TD([[subQ2,-1.0]])],"derivedFrom":subQ1}),-1.0]])]});}
            var Q17;
            {var subQ1=sQuery(id+"F0.wireOp",EDGE,"E12.right");var subQ5=sQuery(id+"F0.wireOp",EDGE,"E0.top");var subQ6=makeQuery(id+"F0.imprint","INTERSECT",VERTEX,{"derivedFrom":[subQ5,subQ1]});Q17=makeQuery(id+"F0.imprint","IMPRINT",FACE,{"disambiguationData":[TD([[makeQuery(id+"F0.imprint","IMPRINT",EDGE,{"disambiguationData":[TD([[subQ6,-1.0]])],"derivedFrom":subQ5}),1.0]])]});}
            var Q18;
            {var subQ0=sQuery(id+"F0.wireOp",EDGE,"E14.left");var subQ1=sQuery(id+"F0.wireOp",EDGE,"E0.bottom");var subQ2=makeQuery(id+"F0.imprint","INTERSECT",VERTEX,{"derivedFrom":[subQ1,subQ0]});Q18=makeQuery(id+"F0.imprint","IMPRINT",FACE,{"disambiguationData":[TD([[makeQuery(id+"F0.imprint","IMPRINT",EDGE,{"disambiguationData":[TD([[subQ2,-1.0]])],"derivedFrom":subQ1}),-1.0]])]});}
            var Q19;
            {var subQ0=sQuery(id+"F0.wireOp",EDGE,"E10");var subQ1=sQuery(id+"F0.wireOp",EDGE,"E0.bottom");var subQ2=makeQuery(id+"F0.imprint","INTERSECT",VERTEX,{"disambiguationData":[OD(1.0)],"derivedFrom":[subQ1,subQ0]});Q19=makeQuery(id+"F0.imprint","IMPRINT",FACE,{"disambiguationData":[TD([[makeQuery(id+"F0.imprint","IMPRINT",EDGE,{"disambiguationData":[TD([[subQ2,-1.0]])],"derivedFrom":subQ1}),-1.0]])]});}
            var Q20;
            {var subQ0=sQuery(id+"F0.wireOp",EDGE,"E16");var subQ1=sQuery(id+"F0.wireOp",EDGE,"E10");var subQ2=makeQuery(id+"F0.imprint","INTERSECT",VERTEX,{"disambiguationData":[OD(0.0)],"derivedFrom":[subQ1,subQ0]});Q20=makeQuery(id+"F0.imprint","IMPRINT",FACE,{"disambiguationData":[TD([[makeQuery(id+"F0.imprint","IMPRINT",EDGE,{"disambiguationData":[TD([[subQ2,-1.0]])],"derivedFrom":subQ1}),1.0]])]});}
            var Q21;
            {var subQ0=sQuery(id+"F0.wireOp",EDGE,"E11.left");var subQ1=sQuery(id+"F0.wireOp",EDGE,"E0.top");var subQ2=makeQuery(id+"F0.imprint","INTERSECT",VERTEX,{"derivedFrom":[subQ1,subQ0]});Q21=makeQuery(id+"F0.imprint","IMPRINT",FACE,{"disambiguationData":[TD([[makeQuery(id+"F0.imprint","IMPRINT",EDGE,{"disambiguationData":[TD([[subQ2,-1.0]])],"derivedFrom":subQ1}),1.0]])]});}
            var Q22;
            {var subQ0=sQuery(id+"F0.wireOp",EDGE,"E7");var subQ1=sQuery(id+"F0.wireOp",EDGE,"E0.top");var subQ2=makeQuery(id+"F0.imprint","INTERSECT",VERTEX,{"disambiguationData":[OD(1.0)],"derivedFrom":[subQ1,subQ0]});Q22=makeQuery(id+"F0.imprint","IMPRINT",FACE,{"disambiguationData":[TD([[makeQuery(id+"F0.imprint","IMPRINT",EDGE,{"disambiguationData":[TD([[subQ2,-1.0]])],"derivedFrom":subQ1}),1.0]])]});}
            var Q23;
            {var subQ0=sQuery(id+"F0.wireOp",EDGE,"E16");var subQ1=sQuery(id+"F0.wireOp",EDGE,"E7");var subQ2=makeQuery(id+"F0.imprint","INTERSECT",VERTEX,{"disambiguationData":[OD(0.0)],"derivedFrom":[subQ1,subQ0]});Q23=makeQuery(id+"F0.imprint","IMPRINT",FACE,{"disambiguationData":[TD([[makeQuery(id+"F0.imprint","IMPRINT",EDGE,{"disambiguationData":[TD([[subQ2,-1.0]])],"derivedFrom":subQ1}),1.0]])]});}
            var Q24;
            {var subQ1=sQuery(id+"F0.wireOp",EDGE,"E11.top");Q24=makeQuery(id+"F0.imprint","IMPRINT",FACE,{"disambiguationData":[TD([[makeQuery(id+"F0.imprint","IMPRINT",EDGE,{"derivedFrom":subQ1}),-1.0]])]});}
            var Q25;
            {var subQ0=sQuery(id+"F0.wireOp",EDGE,"E13.right");var subQ1=sQuery(id+"F0.wireOp",EDGE,"E0.bottom");var subQ2=makeQuery(id+"F0.imprint","INTERSECT",VERTEX,{"derivedFrom":[subQ1,subQ0]});Q25=makeQuery(id+"F0.imprint","IMPRINT",FACE,{"disambiguationData":[TD([[makeQuery(id+"F0.imprint","IMPRINT",EDGE,{"disambiguationData":[TD([[subQ2,-1.0]])],"derivedFrom":subQ1}),-1.0]])]});}
            var Q26;
            {var subQ0=sQuery(id+"F0.wireOp",EDGE,"E9");var subQ1=sQuery(id+"F0.wireOp",EDGE,"E0.bottom");var subQ2=makeQuery(id+"F0.imprint","INTERSECT",VERTEX,{"disambiguationData":[OD(1.0)],"derivedFrom":[subQ1,subQ0]});Q26=makeQuery(id+"F0.imprint","IMPRINT",FACE,{"disambiguationData":[TD([[makeQuery(id+"F0.imprint","IMPRINT",EDGE,{"disambiguationData":[TD([[subQ2,-1.0]])],"derivedFrom":subQ1}),-1.0]])]});}
            var Q27;
            {var subQ0=sQuery(id+"F0.wireOp",EDGE,"E15");var subQ1=sQuery(id+"F0.wireOp",EDGE,"E9");var subQ2=makeQuery(id+"F0.imprint","INTERSECT",VERTEX,{"disambiguationData":[OD(0.0)],"derivedFrom":[subQ1,subQ0]});Q27=makeQuery(id+"F0.imprint","IMPRINT",FACE,{"disambiguationData":[TD([[makeQuery(id+"F0.imprint","IMPRINT",EDGE,{"disambiguationData":[TD([[subQ2,-1.0]])],"derivedFrom":subQ1}),1.0]])]});}
            var Q28;
            {var subQ0=sQuery(id+"F0.wireOp",EDGE,"E12.left");var subQ1=sQuery(id+"F0.wireOp",EDGE,"E0.top");var subQ2=makeQuery(id+"F0.imprint","INTERSECT",VERTEX,{"derivedFrom":[subQ1,subQ0]});Q28=makeQuery(id+"F0.imprint","IMPRINT",FACE,{"disambiguationData":[TD([[makeQuery(id+"F0.imprint","IMPRINT",EDGE,{"disambiguationData":[TD([[subQ2,-1.0]])],"derivedFrom":subQ1}),1.0]])]});}
            var Q29;
            {var subQ0=sQuery(id+"F0.wireOp",EDGE,"E8");var subQ1=sQuery(id+"F0.wireOp",EDGE,"E0.top");var subQ2=makeQuery(id+"F0.imprint","INTERSECT",VERTEX,{"disambiguationData":[OD(1.0)],"derivedFrom":[subQ1,subQ0]});Q29=makeQuery(id+"F0.imprint","IMPRINT",FACE,{"disambiguationData":[TD([[makeQuery(id+"F0.imprint","IMPRINT",EDGE,{"disambiguationData":[TD([[subQ2,-1.0]])],"derivedFrom":subQ1}),1.0]])]});}
            var Q30;
            {var subQ0=sQuery(id+"F0.wireOp",EDGE,"E15");var subQ1=sQuery(id+"F0.wireOp",EDGE,"E8");var subQ2=makeQuery(id+"F0.imprint","INTERSECT",VERTEX,{"disambiguationData":[OD(0.0)],"derivedFrom":[subQ1,subQ0]});Q30=makeQuery(id+"F0.imprint","IMPRINT",FACE,{"disambiguationData":[TD([[makeQuery(id+"F0.imprint","IMPRINT",EDGE,{"disambiguationData":[TD([[subQ2,-1.0]])],"derivedFrom":subQ1}),1.0]])]});}
            var Q31;
            {var subQ8=sQuery(id+"F0.wireOp",EDGE,"E11.right");var subQ10=sQuery(id+"F0.wireOp",EDGE,"E11.top");var subQ11=makeQuery(id+"F0.imprint","INTERSECT",VERTEX,{"derivedFrom":[subQ10,subQ8]});Q31=makeQuery(id+"F0.imprint","IMPRINT",FACE,{"disambiguationData":[TD([[makeQuery(id+"F0.imprint","IMPRINT",EDGE,{"disambiguationData":[TD([[subQ11,1.0]])],"derivedFrom":subQ10}),1.0]])]});}
            var Q32;
            {var subQ6=sQuery(id+"F0.wireOp",EDGE,"E17.right");Q32=makeQuery(id+"F0.imprint","IMPRINT",FACE,{"disambiguationData":[TD([[makeQuery(id+"F0.imprint","IMPRINT",EDGE,{"derivedFrom":subQ6}),1.0]])]});}
            var Q33;
            {var subQ0=sQuery(id+"F0.wireOp",EDGE,"E18");var subQ1=sQuery(id+"F0.wireOp",EDGE,"E11.top");var subQ2=makeQuery(id+"F0.imprint","INTERSECT",VERTEX,{"disambiguationData":[OD(0.0)],"derivedFrom":[subQ1,subQ0]});Q33=makeQuery(id+"F0.imprint","IMPRINT",FACE,{"disambiguationData":[TD([[makeQuery(id+"F0.imprint","IMPRINT",EDGE,{"disambiguationData":[TD([[subQ2,-1.0]])],"derivedFrom":subQ1}),-1.0]])]});}
            var Q34;
            {var subQ0=sQuery(id+"F0.wireOp",EDGE,"E18");var subQ1=sQuery(id+"F0.wireOp",EDGE,"E14.top");var subQ2=makeQuery(id+"F0.imprint","INTERSECT",VERTEX,{"disambiguationData":[OD(0.0)],"derivedFrom":[subQ1,subQ0]});Q34=makeQuery(id+"F0.imprint","IMPRINT",FACE,{"disambiguationData":[TD([[makeQuery(id+"F0.imprint","IMPRINT",EDGE,{"disambiguationData":[TD([[subQ2,-1.0]])],"derivedFrom":subQ1}),1.0]])]});}
            var Q35;
            {var subQ0=sQuery(id+"F0.wireOp",EDGE,"E17.top");var subQ1=sQuery(id+"F0.wireOp",EDGE,"E16");var subQ2=makeQuery(id+"F0.imprint","INTERSECT",VERTEX,{"derivedFrom":[subQ1,subQ0]});Q35=makeQuery(id+"F0.imprint","IMPRINT",FACE,{"disambiguationData":[TD([[makeQuery(id+"F0.imprint","IMPRINT",EDGE,{"disambiguationData":[TD([[subQ2,1.0]])],"derivedFrom":subQ1}),1.0]])]});}
            var Q36;
            {var subQ0=sQuery(id+"F0.wireOp",EDGE,"E17.top");var subQ1=sQuery(id+"F0.wireOp",EDGE,"E15");var subQ2=makeQuery(id+"F0.imprint","INTERSECT",VERTEX,{"derivedFrom":[subQ1,subQ0]});Q36=makeQuery(id+"F0.imprint","IMPRINT",FACE,{"disambiguationData":[TD([[makeQuery(id+"F0.imprint","IMPRINT",EDGE,{"disambiguationData":[TD([[subQ2,-1.0]])],"derivedFrom":subQ1}),1.0]])]});}
            var Q37;
            {var subQ0=sQuery(id+"F0.wireOp",EDGE,"E17.left");Q37=makeQuery(id+"F0.imprint","IMPRINT",FACE,{"disambiguationData":[TD([[makeQuery(id+"F0.imprint","IMPRINT",EDGE,{"derivedFrom":subQ0}),-1.0]])]});}
            var Q38;
            {var subQ7=sQuery(id+"F0.wireOp",EDGE,"E12.left");var subQ8=sQuery(id+"F0.wireOp",EDGE,"E12.top");var subQ9=makeQuery(id+"F0.imprint","INTERSECT",VERTEX,{"derivedFrom":[subQ8,subQ7]});Q38=makeQuery(id+"F0.imprint","IMPRINT",FACE,{"disambiguationData":[TD([[makeQuery(id+"F0.imprint","IMPRINT",EDGE,{"disambiguationData":[TD([[subQ9,-1.0]])],"derivedFrom":subQ8}),1.0]])]});}
            var Q39;
            {var subQ0=sQuery(id+"F0.wireOp",EDGE,"E19");var subQ1=sQuery(id+"F0.wireOp",EDGE,"E12.top");var subQ2=makeQuery(id+"F0.imprint","INTERSECT",VERTEX,{"disambiguationData":[OD(0.0)],"derivedFrom":[subQ1,subQ0]});Q39=makeQuery(id+"F0.imprint","IMPRINT",FACE,{"disambiguationData":[TD([[makeQuery(id+"F0.imprint","IMPRINT",EDGE,{"disambiguationData":[TD([[subQ2,-1.0]])],"derivedFrom":subQ1}),-1.0]])]});}
            var Q40;
            {var subQ0=sQuery(id+"F0.wireOp",EDGE,"E19");var subQ1=sQuery(id+"F0.wireOp",EDGE,"E13.top");var subQ2=makeQuery(id+"F0.imprint","INTERSECT",VERTEX,{"disambiguationData":[OD(0.0)],"derivedFrom":[subQ1,subQ0]});Q40=makeQuery(id+"F0.imprint","IMPRINT",FACE,{"disambiguationData":[TD([[makeQuery(id+"F0.imprint","IMPRINT",EDGE,{"disambiguationData":[TD([[subQ2,-1.0]])],"derivedFrom":subQ1}),-1.0]])]});}
            var Q41;
            {var subQ5=sQuery(id+"F0.wireOp",EDGE,"E13.left");var subQ6=sQuery(id+"F0.wireOp",EDGE,"E13.top");var subQ7=makeQuery(id+"F0.imprint","INTERSECT",VERTEX,{"derivedFrom":[subQ6,subQ5]});Q41=makeQuery(id+"F0.imprint","IMPRINT",FACE,{"disambiguationData":[TD([[makeQuery(id+"F0.imprint","IMPRINT",EDGE,{"disambiguationData":[TD([[subQ7,-1.0]])],"derivedFrom":subQ6}),1.0]])]});}
            var Q42;
            {var subQ5=sQuery(id+"F0.wireOp",EDGE,"E14.left");var subQ7=sQuery(id+"F0.wireOp",EDGE,"E14.top");var subQ8=makeQuery(id+"F0.imprint","INTERSECT",VERTEX,{"derivedFrom":[subQ7,subQ5]});Q42=makeQuery(id+"F0.imprint","IMPRINT",FACE,{"disambiguationData":[TD([[makeQuery(id+"F0.imprint","IMPRINT",EDGE,{"disambiguationData":[TD([[subQ8,-1.0]])],"derivedFrom":subQ7}),-1.0]])]});}
            extrude(context, id + "F2", {"entities" : qUnion([Q0, Q1, Q2, Q3, Q4, Q5, Q6, Q7, Q8, Q9, Q10, Q11, Q12, Q13, Q14, Q15, Q16, Q17, Q18, Q19, Q20, Q21, Q22, Q23, Q24, Q25, Q26, Q27, Q28, Q29, Q30, Q31, Q32, Q33, Q34, Q35, Q36, Q37, Q38, Q39, Q40, Q41, Q42]), "operationType" : NewBodyOperationType.ADD, "depth" : 11.94 * mm, "offsetDistance" : 25.4 * mm});
        }
        {
            var Q0;
            {var subQ8=sQuery(id+"F0.wireOp",EDGE,"E11.right");var subQ10=sQuery(id+"F0.wireOp",EDGE,"E11.top");var subQ11=makeQuery(id+"F0.imprint","INTERSECT",VERTEX,{"derivedFrom":[subQ10,subQ8]});Q0=makeQuery(id+"F0.imprint","IMPRINT",FACE,{"disambiguationData":[TD([[makeQuery(id+"F0.imprint","IMPRINT",EDGE,{"disambiguationData":[TD([[subQ11,1.0]])],"derivedFrom":subQ10}),1.0]])]});}
            var Q1;
            {var subQ5=sQuery(id+"F0.wireOp",EDGE,"E16");var subQ6=sQuery(id+"F0.wireOp",EDGE,"E7");var subQ12=makeQuery(id+"F0.imprint","INTERSECT",VERTEX,{"disambiguationData":[OD(0.0)],"derivedFrom":[subQ6,subQ5]});Q1=makeQuery(id+"F0.imprint","IMPRINT",FACE,{"disambiguationData":[TD([[makeQuery(id+"F0.imprint","IMPRINT",EDGE,{"disambiguationData":[TD([[subQ12,-1.0]])],"derivedFrom":subQ6}),-1.0]])]});}
            var Q2;
            {var subQ1=sQuery(id+"F0.wireOp",EDGE,"E11.left");var subQ7=sQuery(id+"F0.wireOp",EDGE,"E11.top");var subQ8=makeQuery(id+"F0.imprint","INTERSECT",VERTEX,{"derivedFrom":[subQ7,subQ1]});Q2=makeQuery(id+"F0.imprint","IMPRINT",FACE,{"disambiguationData":[TD([[makeQuery(id+"F0.imprint","IMPRINT",EDGE,{"disambiguationData":[TD([[subQ8,-1.0]])],"derivedFrom":subQ7}),1.0]])]});}
            var Q3;
            {var subQ0=sQuery(id+"F0.wireOp",EDGE,"E17.top");var subQ1=sQuery(id+"F0.wireOp",EDGE,"E16");var subQ2=makeQuery(id+"F0.imprint","INTERSECT",VERTEX,{"derivedFrom":[subQ1,subQ0]});Q3=makeQuery(id+"F0.imprint","IMPRINT",FACE,{"disambiguationData":[TD([[makeQuery(id+"F0.imprint","IMPRINT",EDGE,{"disambiguationData":[TD([[subQ2,1.0]])],"derivedFrom":subQ1}),1.0]])]});}
            var Q4;
            {var subQ0=sQuery(id+"F0.wireOp",EDGE,"E17.top");var subQ1=sQuery(id+"F0.wireOp",EDGE,"E15");var subQ2=makeQuery(id+"F0.imprint","INTERSECT",VERTEX,{"derivedFrom":[subQ1,subQ0]});Q4=makeQuery(id+"F0.imprint","IMPRINT",FACE,{"disambiguationData":[TD([[makeQuery(id+"F0.imprint","IMPRINT",EDGE,{"disambiguationData":[TD([[subQ2,-1.0]])],"derivedFrom":subQ1}),-1.0]])]});}
            var Q5;
            {var subQ5=sQuery(id+"F0.wireOp",EDGE,"E14.left");var subQ7=sQuery(id+"F0.wireOp",EDGE,"E14.top");var subQ8=makeQuery(id+"F0.imprint","INTERSECT",VERTEX,{"derivedFrom":[subQ7,subQ5]});Q5=makeQuery(id+"F0.imprint","IMPRINT",FACE,{"disambiguationData":[TD([[makeQuery(id+"F0.imprint","IMPRINT",EDGE,{"disambiguationData":[TD([[subQ8,-1.0]])],"derivedFrom":subQ7}),-1.0]])]});}
            var Q6;
            {var subQ8=sQuery(id+"F0.wireOp",EDGE,"E16");var subQ10=sQuery(id+"F0.wireOp",EDGE,"E10");var subQ11=makeQuery(id+"F0.imprint","INTERSECT",VERTEX,{"disambiguationData":[OD(0.0)],"derivedFrom":[subQ10,subQ8]});Q6=makeQuery(id+"F0.imprint","IMPRINT",FACE,{"disambiguationData":[TD([[makeQuery(id+"F0.imprint","IMPRINT",EDGE,{"disambiguationData":[TD([[subQ11,-1.0]])],"derivedFrom":subQ10}),-1.0]])]});}
            var Q7;
            {var subQ0=sQuery(id+"F0.wireOp",EDGE,"E17.top");var subQ1=sQuery(id+"F0.wireOp",EDGE,"E15");var subQ2=makeQuery(id+"F0.imprint","INTERSECT",VERTEX,{"derivedFrom":[subQ1,subQ0]});Q7=makeQuery(id+"F0.imprint","IMPRINT",FACE,{"disambiguationData":[TD([[makeQuery(id+"F0.imprint","IMPRINT",EDGE,{"disambiguationData":[TD([[subQ2,-1.0]])],"derivedFrom":subQ1}),1.0]])]});}
            var Q8;
            {var subQ5=sQuery(id+"F0.wireOp",EDGE,"E12.right");var subQ6=sQuery(id+"F0.wireOp",EDGE,"E12.top");var subQ7=makeQuery(id+"F0.imprint","INTERSECT",VERTEX,{"derivedFrom":[subQ6,subQ5]});Q8=makeQuery(id+"F0.imprint","IMPRINT",FACE,{"disambiguationData":[TD([[makeQuery(id+"F0.imprint","IMPRINT",EDGE,{"disambiguationData":[TD([[subQ7,1.0]])],"derivedFrom":subQ6}),1.0]])]});}
            var Q9;
            {var subQ7=sQuery(id+"F0.wireOp",EDGE,"E12.left");var subQ8=sQuery(id+"F0.wireOp",EDGE,"E12.top");var subQ9=makeQuery(id+"F0.imprint","INTERSECT",VERTEX,{"derivedFrom":[subQ8,subQ7]});Q9=makeQuery(id+"F0.imprint","IMPRINT",FACE,{"disambiguationData":[TD([[makeQuery(id+"F0.imprint","IMPRINT",EDGE,{"disambiguationData":[TD([[subQ9,-1.0]])],"derivedFrom":subQ8}),1.0]])]});}
            var Q10;
            {var subQ7=sQuery(id+"F0.wireOp",EDGE,"E15");var subQ9=sQuery(id+"F0.wireOp",EDGE,"E9");var subQ10=makeQuery(id+"F0.imprint","INTERSECT",VERTEX,{"disambiguationData":[OD(0.0)],"derivedFrom":[subQ9,subQ7]});Q10=makeQuery(id+"F0.imprint","IMPRINT",FACE,{"disambiguationData":[TD([[makeQuery(id+"F0.imprint","IMPRINT",EDGE,{"disambiguationData":[TD([[subQ10,-1.0]])],"derivedFrom":subQ9}),-1.0]])]});}
            var Q11;
            {var subQ5=sQuery(id+"F0.wireOp",EDGE,"E13.left");var subQ6=sQuery(id+"F0.wireOp",EDGE,"E13.top");var subQ7=makeQuery(id+"F0.imprint","INTERSECT",VERTEX,{"derivedFrom":[subQ6,subQ5]});Q11=makeQuery(id+"F0.imprint","IMPRINT",FACE,{"disambiguationData":[TD([[makeQuery(id+"F0.imprint","IMPRINT",EDGE,{"disambiguationData":[TD([[subQ7,-1.0]])],"derivedFrom":subQ6}),1.0]])]});}
            var Q12;
            {var subQ0=sQuery(id+"F0.wireOp",EDGE,"E16");var subQ1=sQuery(id+"F0.wireOp",EDGE,"E10");var subQ2=makeQuery(id+"F0.imprint","INTERSECT",VERTEX,{"disambiguationData":[OD(0.0)],"derivedFrom":[subQ1,subQ0]});Q12=makeQuery(id+"F0.imprint","IMPRINT",FACE,{"disambiguationData":[TD([[makeQuery(id+"F0.imprint","IMPRINT",EDGE,{"disambiguationData":[TD([[subQ2,-1.0]])],"derivedFrom":subQ1}),1.0]])]});}
            var Q13;
            {var subQ0=sQuery(id+"F0.wireOp",EDGE,"E15");var subQ1=sQuery(id+"F0.wireOp",EDGE,"E9");var subQ2=makeQuery(id+"F0.imprint","INTERSECT",VERTEX,{"disambiguationData":[OD(0.0)],"derivedFrom":[subQ1,subQ0]});Q13=makeQuery(id+"F0.imprint","IMPRINT",FACE,{"disambiguationData":[TD([[makeQuery(id+"F0.imprint","IMPRINT",EDGE,{"disambiguationData":[TD([[subQ2,-1.0]])],"derivedFrom":subQ1}),1.0]])]});}
            var Q14;
            {var subQ0=sQuery(id+"F0.wireOp",EDGE,"E15");var subQ1=sQuery(id+"F0.wireOp",EDGE,"E8");var subQ2=makeQuery(id+"F0.imprint","INTERSECT",VERTEX,{"disambiguationData":[OD(0.0)],"derivedFrom":[subQ1,subQ0]});Q14=makeQuery(id+"F0.imprint","IMPRINT",FACE,{"disambiguationData":[TD([[makeQuery(id+"F0.imprint","IMPRINT",EDGE,{"disambiguationData":[TD([[subQ2,-1.0]])],"derivedFrom":subQ1}),1.0]])]});}
            var Q15;
            {var subQ0=sQuery(id+"F0.wireOp",EDGE,"E16");var subQ1=sQuery(id+"F0.wireOp",EDGE,"E7");var subQ2=makeQuery(id+"F0.imprint","INTERSECT",VERTEX,{"disambiguationData":[OD(0.0)],"derivedFrom":[subQ1,subQ0]});Q15=makeQuery(id+"F0.imprint","IMPRINT",FACE,{"disambiguationData":[TD([[makeQuery(id+"F0.imprint","IMPRINT",EDGE,{"disambiguationData":[TD([[subQ2,-1.0]])],"derivedFrom":subQ1}),1.0]])]});}
            var Q16;
            {var subQ6=sQuery(id+"F0.wireOp",EDGE,"E17.right");Q16=makeQuery(id+"F0.imprint","IMPRINT",FACE,{"disambiguationData":[TD([[makeQuery(id+"F0.imprint","IMPRINT",EDGE,{"derivedFrom":subQ6}),1.0]])]});}
            var Q17;
            {var subQ0=sQuery(id+"F0.wireOp",EDGE,"E17.left");Q17=makeQuery(id+"F0.imprint","IMPRINT",FACE,{"disambiguationData":[TD([[makeQuery(id+"F0.imprint","IMPRINT",EDGE,{"derivedFrom":subQ0}),-1.0]])]});}
            var Q18;
            {var subQ0=sQuery(id+"F0.wireOp",EDGE,"E17.left");Q18=makeQuery(id+"F0.imprint","IMPRINT",FACE,{"disambiguationData":[TD([[makeQuery(id+"F0.imprint","IMPRINT",EDGE,{"derivedFrom":subQ0}),1.0]])]});}
            var Q19;
            {var subQ0=sQuery(id+"F0.wireOp",EDGE,"E17.right");Q19=makeQuery(id+"F0.imprint","IMPRINT",FACE,{"disambiguationData":[TD([[makeQuery(id+"F0.imprint","IMPRINT",EDGE,{"derivedFrom":subQ0}),-1.0]])]});}
            var Q20;
            {var subQ0=sQuery(id+"F0.wireOp",EDGE,"E18");var subQ1=sQuery(id+"F0.wireOp",EDGE,"E14.top");var subQ2=makeQuery(id+"F0.imprint","INTERSECT",VERTEX,{"disambiguationData":[OD(0.0)],"derivedFrom":[subQ1,subQ0]});Q20=makeQuery(id+"F0.imprint","IMPRINT",FACE,{"disambiguationData":[TD([[makeQuery(id+"F0.imprint","IMPRINT",EDGE,{"disambiguationData":[TD([[subQ2,-1.0]])],"derivedFrom":subQ1}),1.0]])]});}
            var Q21;
            {var subQ0=sQuery(id+"F0.wireOp",EDGE,"E18");var subQ1=sQuery(id+"F0.wireOp",EDGE,"E11.top");var subQ2=makeQuery(id+"F0.imprint","INTERSECT",VERTEX,{"disambiguationData":[OD(0.0)],"derivedFrom":[subQ1,subQ0]});Q21=makeQuery(id+"F0.imprint","IMPRINT",FACE,{"disambiguationData":[TD([[makeQuery(id+"F0.imprint","IMPRINT",EDGE,{"disambiguationData":[TD([[subQ2,-1.0]])],"derivedFrom":subQ1}),-1.0]])]});}
            var Q22;
            {var subQ0=sQuery(id+"F0.wireOp",EDGE,"E19");var subQ1=sQuery(id+"F0.wireOp",EDGE,"E13.top");var subQ2=makeQuery(id+"F0.imprint","INTERSECT",VERTEX,{"disambiguationData":[OD(0.0)],"derivedFrom":[subQ1,subQ0]});Q22=makeQuery(id+"F0.imprint","IMPRINT",FACE,{"disambiguationData":[TD([[makeQuery(id+"F0.imprint","IMPRINT",EDGE,{"disambiguationData":[TD([[subQ2,-1.0]])],"derivedFrom":subQ1}),-1.0]])]});}
            var Q23;
            {var subQ7=sQuery(id+"F0.wireOp",EDGE,"E15");var subQ10=sQuery(id+"F0.wireOp",EDGE,"E8");var subQ11=makeQuery(id+"F0.imprint","INTERSECT",VERTEX,{"disambiguationData":[OD(0.0)],"derivedFrom":[subQ10,subQ7]});Q23=makeQuery(id+"F0.imprint","IMPRINT",FACE,{"disambiguationData":[TD([[makeQuery(id+"F0.imprint","IMPRINT",EDGE,{"disambiguationData":[TD([[subQ11,-1.0]])],"derivedFrom":subQ10}),-1.0]])]});}
            var Q24;
            {var subQ0=sQuery(id+"F0.wireOp",EDGE,"E19");var subQ1=sQuery(id+"F0.wireOp",EDGE,"E12.top");var subQ2=makeQuery(id+"F0.imprint","INTERSECT",VERTEX,{"disambiguationData":[OD(0.0)],"derivedFrom":[subQ1,subQ0]});Q24=makeQuery(id+"F0.imprint","IMPRINT",FACE,{"disambiguationData":[TD([[makeQuery(id+"F0.imprint","IMPRINT",EDGE,{"disambiguationData":[TD([[subQ2,-1.0]])],"derivedFrom":subQ1}),-1.0]])]});}
            extrude(context, id + "F3", {"entities" : qUnion([Q0, Q1, Q2, Q3, Q4, Q5, Q6, Q7, Q8, Q9, Q10, Q11, Q12, Q13, Q14, Q15, Q16, Q17, Q18, Q19, Q20, Q21, Q22, Q23, Q24]), "operationType" : NewBodyOperationType.ADD, "depth" : 34 * mm, "offsetDistance" : 25.4 * mm});
        }
        {
            var Q0;
            {var subQ8=sQuery(id+"F0.wireOp",EDGE,"E11.right");var subQ10=sQuery(id+"F0.wireOp",EDGE,"E11.top");var subQ11=makeQuery(id+"F0.imprint","INTERSECT",VERTEX,{"derivedFrom":[subQ10,subQ8]});Q0=makeQuery(id+"F0.imprint","IMPRINT",FACE,{"disambiguationData":[TD([[makeQuery(id+"F0.imprint","IMPRINT",EDGE,{"disambiguationData":[TD([[subQ11,1.0]])],"derivedFrom":subQ10}),1.0]])]});}
            var Q1;
            {var subQ0=sQuery(id+"F0.wireOp",EDGE,"E17.top");var subQ1=sQuery(id+"F0.wireOp",EDGE,"E16");var subQ2=makeQuery(id+"F0.imprint","INTERSECT",VERTEX,{"derivedFrom":[subQ1,subQ0]});Q1=makeQuery(id+"F0.imprint","IMPRINT",FACE,{"disambiguationData":[TD([[makeQuery(id+"F0.imprint","IMPRINT",EDGE,{"disambiguationData":[TD([[subQ2,1.0]])],"derivedFrom":subQ1}),1.0]])]});}
            var Q2;
            {var subQ0=sQuery(id+"F0.wireOp",EDGE,"E17.top");var subQ1=sQuery(id+"F0.wireOp",EDGE,"E15");var subQ2=makeQuery(id+"F0.imprint","INTERSECT",VERTEX,{"derivedFrom":[subQ1,subQ0]});Q2=makeQuery(id+"F0.imprint","IMPRINT",FACE,{"disambiguationData":[TD([[makeQuery(id+"F0.imprint","IMPRINT",EDGE,{"disambiguationData":[TD([[subQ2,-1.0]])],"derivedFrom":subQ1}),1.0]])]});}
            var Q3;
            {var subQ7=sQuery(id+"F0.wireOp",EDGE,"E12.left");var subQ8=sQuery(id+"F0.wireOp",EDGE,"E12.top");var subQ9=makeQuery(id+"F0.imprint","INTERSECT",VERTEX,{"derivedFrom":[subQ8,subQ7]});Q3=makeQuery(id+"F0.imprint","IMPRINT",FACE,{"disambiguationData":[TD([[makeQuery(id+"F0.imprint","IMPRINT",EDGE,{"disambiguationData":[TD([[subQ9,-1.0]])],"derivedFrom":subQ8}),1.0]])]});}
            var Q4;
            {var subQ7=sQuery(id+"F0.wireOp",EDGE,"E15");var subQ10=sQuery(id+"F0.wireOp",EDGE,"E8");var subQ11=makeQuery(id+"F0.imprint","INTERSECT",VERTEX,{"disambiguationData":[OD(0.0)],"derivedFrom":[subQ10,subQ7]});Q4=makeQuery(id+"F0.imprint","IMPRINT",FACE,{"disambiguationData":[TD([[makeQuery(id+"F0.imprint","IMPRINT",EDGE,{"disambiguationData":[TD([[subQ11,-1.0]])],"derivedFrom":subQ10}),-1.0]])]});}
            var Q5;
            {var subQ5=sQuery(id+"F0.wireOp",EDGE,"E13.left");var subQ6=sQuery(id+"F0.wireOp",EDGE,"E13.top");var subQ7=makeQuery(id+"F0.imprint","INTERSECT",VERTEX,{"derivedFrom":[subQ6,subQ5]});Q5=makeQuery(id+"F0.imprint","IMPRINT",FACE,{"disambiguationData":[TD([[makeQuery(id+"F0.imprint","IMPRINT",EDGE,{"disambiguationData":[TD([[subQ7,-1.0]])],"derivedFrom":subQ6}),1.0]])]});}
            var Q6;
            {var subQ7=sQuery(id+"F0.wireOp",EDGE,"E15");var subQ9=sQuery(id+"F0.wireOp",EDGE,"E9");var subQ10=makeQuery(id+"F0.imprint","INTERSECT",VERTEX,{"disambiguationData":[OD(0.0)],"derivedFrom":[subQ9,subQ7]});Q6=makeQuery(id+"F0.imprint","IMPRINT",FACE,{"disambiguationData":[TD([[makeQuery(id+"F0.imprint","IMPRINT",EDGE,{"disambiguationData":[TD([[subQ10,-1.0]])],"derivedFrom":subQ9}),-1.0]])]});}
            var Q7;
            {var subQ5=sQuery(id+"F0.wireOp",EDGE,"E14.left");var subQ7=sQuery(id+"F0.wireOp",EDGE,"E14.top");var subQ8=makeQuery(id+"F0.imprint","INTERSECT",VERTEX,{"derivedFrom":[subQ7,subQ5]});Q7=makeQuery(id+"F0.imprint","IMPRINT",FACE,{"disambiguationData":[TD([[makeQuery(id+"F0.imprint","IMPRINT",EDGE,{"disambiguationData":[TD([[subQ8,-1.0]])],"derivedFrom":subQ7}),-1.0]])]});}
            var Q8;
            {var subQ8=sQuery(id+"F0.wireOp",EDGE,"E16");var subQ10=sQuery(id+"F0.wireOp",EDGE,"E10");var subQ11=makeQuery(id+"F0.imprint","INTERSECT",VERTEX,{"disambiguationData":[OD(0.0)],"derivedFrom":[subQ10,subQ8]});Q8=makeQuery(id+"F0.imprint","IMPRINT",FACE,{"disambiguationData":[TD([[makeQuery(id+"F0.imprint","IMPRINT",EDGE,{"disambiguationData":[TD([[subQ11,-1.0]])],"derivedFrom":subQ10}),-1.0]])]});}
            var Q9;
            {var subQ5=sQuery(id+"F0.wireOp",EDGE,"E16");var subQ6=sQuery(id+"F0.wireOp",EDGE,"E7");var subQ12=makeQuery(id+"F0.imprint","INTERSECT",VERTEX,{"disambiguationData":[OD(0.0)],"derivedFrom":[subQ6,subQ5]});Q9=makeQuery(id+"F0.imprint","IMPRINT",FACE,{"disambiguationData":[TD([[makeQuery(id+"F0.imprint","IMPRINT",EDGE,{"disambiguationData":[TD([[subQ12,-1.0]])],"derivedFrom":subQ6}),-1.0]])]});}
            var Q10;
            {var subQ1=sQuery(id+"F0.wireOp",EDGE,"E11.left");var subQ7=sQuery(id+"F0.wireOp",EDGE,"E11.top");var subQ8=makeQuery(id+"F0.imprint","INTERSECT",VERTEX,{"derivedFrom":[subQ7,subQ1]});Q10=makeQuery(id+"F0.imprint","IMPRINT",FACE,{"disambiguationData":[TD([[makeQuery(id+"F0.imprint","IMPRINT",EDGE,{"disambiguationData":[TD([[subQ8,-1.0]])],"derivedFrom":subQ7}),1.0]])]});}
            var Q11;
            {var subQ5=sQuery(id+"F0.wireOp",EDGE,"E12.right");var subQ6=sQuery(id+"F0.wireOp",EDGE,"E12.top");var subQ7=makeQuery(id+"F0.imprint","INTERSECT",VERTEX,{"derivedFrom":[subQ6,subQ5]});Q11=makeQuery(id+"F0.imprint","IMPRINT",FACE,{"disambiguationData":[TD([[makeQuery(id+"F0.imprint","IMPRINT",EDGE,{"disambiguationData":[TD([[subQ7,1.0]])],"derivedFrom":subQ6}),1.0]])]});}
            var Q12;
            {var subQ0=sQuery(id+"F0.wireOp",EDGE,"E15");var subQ1=sQuery(id+"F0.wireOp",EDGE,"E9");var subQ2=makeQuery(id+"F0.imprint","INTERSECT",VERTEX,{"disambiguationData":[OD(0.0)],"derivedFrom":[subQ1,subQ0]});Q12=makeQuery(id+"F0.imprint","IMPRINT",FACE,{"disambiguationData":[TD([[makeQuery(id+"F0.imprint","IMPRINT",EDGE,{"disambiguationData":[TD([[subQ2,-1.0]])],"derivedFrom":subQ1}),1.0]])]});}
            var Q13;
            {var subQ0=sQuery(id+"F0.wireOp",EDGE,"E16");var subQ1=sQuery(id+"F0.wireOp",EDGE,"E10");var subQ2=makeQuery(id+"F0.imprint","INTERSECT",VERTEX,{"disambiguationData":[OD(0.0)],"derivedFrom":[subQ1,subQ0]});Q13=makeQuery(id+"F0.imprint","IMPRINT",FACE,{"disambiguationData":[TD([[makeQuery(id+"F0.imprint","IMPRINT",EDGE,{"disambiguationData":[TD([[subQ2,-1.0]])],"derivedFrom":subQ1}),1.0]])]});}
            var Q14;
            {var subQ0=sQuery(id+"F0.wireOp",EDGE,"E16");var subQ1=sQuery(id+"F0.wireOp",EDGE,"E7");var subQ2=makeQuery(id+"F0.imprint","INTERSECT",VERTEX,{"disambiguationData":[OD(0.0)],"derivedFrom":[subQ1,subQ0]});Q14=makeQuery(id+"F0.imprint","IMPRINT",FACE,{"disambiguationData":[TD([[makeQuery(id+"F0.imprint","IMPRINT",EDGE,{"disambiguationData":[TD([[subQ2,-1.0]])],"derivedFrom":subQ1}),1.0]])]});}
            var Q15;
            {var subQ0=sQuery(id+"F0.wireOp",EDGE,"E15");var subQ1=sQuery(id+"F0.wireOp",EDGE,"E8");var subQ2=makeQuery(id+"F0.imprint","INTERSECT",VERTEX,{"disambiguationData":[OD(0.0)],"derivedFrom":[subQ1,subQ0]});Q15=makeQuery(id+"F0.imprint","IMPRINT",FACE,{"disambiguationData":[TD([[makeQuery(id+"F0.imprint","IMPRINT",EDGE,{"disambiguationData":[TD([[subQ2,-1.0]])],"derivedFrom":subQ1}),1.0]])]});}
            extrude(context, id + "F4", {"entities" : qUnion([Q0, Q1, Q2, Q3, Q4, Q5, Q6, Q7, Q8, Q9, Q10, Q11, Q12, Q13, Q14, Q15]), "operationType" : NewBodyOperationType.ADD, "depth" : 37.34 * mm, "offsetDistance" : 25.4 * mm});
        }
        {
            var Q0;
            {var subQ0=sQuery(id+"F0.wireOp",EDGE,"E1.left");var subQ1=sQuery(id+"F0.wireOp",EDGE,"E0.bottom");Q0=makeQuery(id+"F2.boolean.opBoolean","MERGE",EDGE,{"derivedFrom":[makeQuery(id+"F1.opExtrude","SWEPT_EDGE",EDGE,{"disambiguationData":[OSD([subQ1,subQ0])]}),makeQuery(id+"F2.opExtrude","SWEPT_EDGE",EDGE,{"disambiguationData":[OSD([subQ1,subQ0])]})]});}
            var Q1;
            {var subQ0=sQuery(id+"F0.wireOp",EDGE,"E1.left");var subQ1=sQuery(id+"F0.wireOp",EDGE,"E0.top");Q1=makeQuery(id+"F2.boolean.opBoolean","MERGE",EDGE,{"derivedFrom":[makeQuery(id+"F1.opExtrude","SWEPT_EDGE",EDGE,{"disambiguationData":[OSD([subQ1,subQ0])]}),makeQuery(id+"F2.opExtrude","SWEPT_EDGE",EDGE,{"disambiguationData":[OSD([subQ1,subQ0])]})]});}
            var Q2;
            {var subQ0=sQuery(id+"F0.wireOp",EDGE,"E1.right");var subQ1=sQuery(id+"F0.wireOp",EDGE,"E0.bottom");Q2=makeQuery(id+"F2.boolean.opBoolean","MERGE",EDGE,{"derivedFrom":[makeQuery(id+"F1.opExtrude","SWEPT_EDGE",EDGE,{"disambiguationData":[OSD([subQ1,subQ0])]}),makeQuery(id+"F2.opExtrude","SWEPT_EDGE",EDGE,{"disambiguationData":[OSD([subQ1,subQ0])]})]});}
            var Q3;
            {var subQ0=sQuery(id+"F0.wireOp",EDGE,"E1.right");var subQ1=sQuery(id+"F0.wireOp",EDGE,"E0.top");Q3=makeQuery(id+"F2.boolean.opBoolean","MERGE",EDGE,{"derivedFrom":[makeQuery(id+"F1.opExtrude","SWEPT_EDGE",EDGE,{"disambiguationData":[OSD([subQ1,subQ0])]}),makeQuery(id+"F2.opExtrude","SWEPT_EDGE",EDGE,{"disambiguationData":[OSD([subQ1,subQ0])]})]});}
            fillet(context, id + "F5", {"entities" : qUnion([Q0, Q1, Q2, Q3]), "radius" : 1 * mm, "tangentPropagation" : true, "allowEdgeOverflow" : false});
        }
        {
            var Q0;
            Q0=makeQuery(id+"F1.opExtrude","SWEPT_EDGE",EDGE,{"disambiguationData":[OSD([sQuery(id+"F0.wireOp",EDGE,"E0.bottom"),sQuery(id+"F0.wireOp",EDGE,"E14.right")])]});
            var Q1;
            Q1=makeQuery(id+"F1.opExtrude","SWEPT_EDGE",EDGE,{"disambiguationData":[OSD([sQuery(id+"F0.wireOp",EDGE,"E0.bottom"),sQuery(id+"F0.wireOp",EDGE,"E13.left")])]});
            var Q2;
            Q2=makeQuery(id+"F1.opExtrude","SWEPT_EDGE",EDGE,{"disambiguationData":[OSD([sQuery(id+"F0.wireOp",EDGE,"E0.bottom"),sQuery(id+"F0.wireOp",EDGE,"E14.left")])]});
            var Q3;
            Q3=makeQuery(id+"F1.opExtrude","SWEPT_EDGE",EDGE,{"disambiguationData":[OSD([sQuery(id+"F0.wireOp",EDGE,"E0.bottom"),sQuery(id+"F0.wireOp",EDGE,"E13.right")])]});
            var Q4;
            Q4=makeQuery(id+"F1.opExtrude","SWEPT_EDGE",EDGE,{"disambiguationData":[OSD([sQuery(id+"F0.wireOp",EDGE,"E0.top"),sQuery(id+"F0.wireOp",EDGE,"E12.left")])]});
            var Q5;
            Q5=makeQuery(id+"F1.opExtrude","SWEPT_EDGE",EDGE,{"disambiguationData":[OSD([sQuery(id+"F0.wireOp",EDGE,"E0.top"),sQuery(id+"F0.wireOp",EDGE,"E11.left")])]});
            var Q6;
            Q6=makeQuery(id+"F1.opExtrude","SWEPT_EDGE",EDGE,{"disambiguationData":[OSD([sQuery(id+"F0.wireOp",EDGE,"E0.top"),sQuery(id+"F0.wireOp",EDGE,"E12.right")])]});
            var Q7;
            Q7=makeQuery(id+"F1.opExtrude","SWEPT_EDGE",EDGE,{"disambiguationData":[OSD([sQuery(id+"F0.wireOp",EDGE,"E0.top"),sQuery(id+"F0.wireOp",EDGE,"E11.right")])]});
            fillet(context, id + "F6", {"entities" : qUnion([Q0, Q1, Q2, Q3, Q4, Q5, Q6, Q7]), "radius" : 2 * mm, "tangentPropagation" : true, "allowEdgeOverflow" : false});
        }
        {
            var Q0;
            Q0=makeQuery(id+"F3.opExtrude","SWEPT_EDGE",EDGE,{"disambiguationData":[OSD([sQuery(id+"F0.wireOp",EDGE,"E15"),sQuery(id+"F0.wireOp",EDGE,"E17.top")])]});
            var Q1;
            Q1=makeQuery(id+"F3.opExtrude","SWEPT_EDGE",EDGE,{"disambiguationData":[OSD([sQuery(id+"F0.wireOp",EDGE,"E16"),sQuery(id+"F0.wireOp",EDGE,"E17.top")])]});
            var Q2;
            Q2=makeQuery(id+"F3.opExtrude","SWEPT_EDGE",EDGE,{"disambiguationData":[OSD([sQuery(id+"F0.wireOp",EDGE,"E16"),sQuery(id+"F0.wireOp",EDGE,"E17.bottom")])]});
            var Q3;
            Q3=makeQuery(id+"F3.opExtrude","SWEPT_EDGE",EDGE,{"disambiguationData":[OSD([sQuery(id+"F0.wireOp",EDGE,"E15"),sQuery(id+"F0.wireOp",EDGE,"E17.bottom")])]});
            fillet(context, id + "F7", {"entities" : qUnion([Q0, Q1, Q2, Q3]), "radius" : 2.54 * mm, "tangentPropagation" : true, "allowEdgeOverflow" : false});
        }
    });
